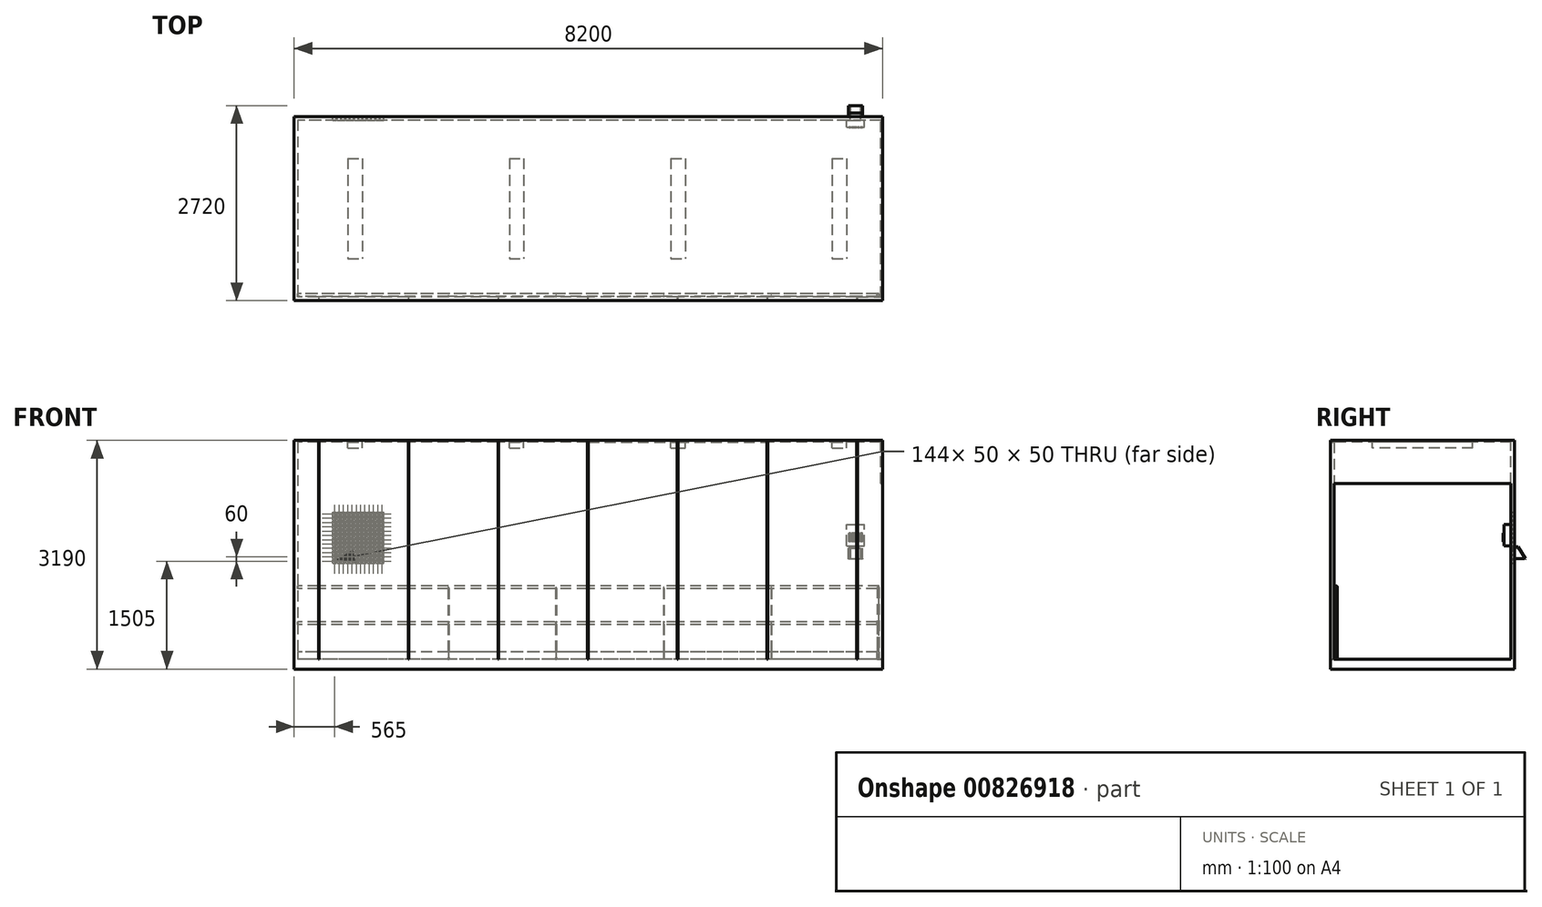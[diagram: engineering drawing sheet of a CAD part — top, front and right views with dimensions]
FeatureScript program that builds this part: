
annotation { "Feature Type Name" : "Feature", "Feature Type Description" : "" }
export const myFeature = defineFeature(function(context is Context, id is Id, definition is map)
    precondition{}
    {
        {
            var Q0;
            Q0=qCreatedBy(makeId("Top.planeOp"),FACE);
            var sketch = newSketch(context, id + "F0", { "sketchPlane" : qUnion([Q0])});
            skLineSegment(sketch, "E0.bottom", {"start": v(4100, -1285) * mm, "end": v(-4100, -1285) * mm});
            skLineSegment(sketch, "E0.top", {"start": v(4100, 1285) * mm, "end": v(-4100, 1285) * mm});
            skLineSegment(sketch, "E0.left", {"start": v(4100, -1285) * mm, "end": v(4100, 1285) * mm});
            skLineSegment(sketch, "E0.right", {"start": v(-4100, -1285) * mm, "end": v(-4100, 1285) * mm});
            skPoint(sketch, "E0.middle", {"position": v(0, 0) * mm});
            skSolve(sketch);
        }
        {
            var Q0;
            Q0=makeQuery(id+"F0.imprint","IMPRINT",FACE,{"disambiguationData":[TD([[makeQuery(id+"F0.imprint","IMPRINT",EDGE,{"derivedFrom":sQuery(id+"F0.wireOp",EDGE,"E0.bottom")}),-1.0]])]});
            extrude(context, id + "F1", {"entities" : qUnion([Q0]), "depth" : 25 * mm, "offsetDistance" : 25 * mm});
        }
        {
            var Q0;
            Q0=makeQuery(id+"F1.opExtrude","CAP_FACE",FACE,{"disambiguationData":[OSD([sQuery(id+"F0.wireOp",EDGE,"E0.bottom"),sQuery(id+"F0.wireOp",EDGE,"E0.top"),sQuery(id+"F0.wireOp",EDGE,"E0.left"),sQuery(id+"F0.wireOp",EDGE,"E0.right")])],"isStart":false});
            var sketch = newSketch(context, id + "F2", { "sketchPlane" : qUnion([Q0])});
            skLineSegment(sketch, "E1.bottom", {"start": v(4100, 1285) * mm, "end": v(-4100, 1285) * mm});
            skLineSegment(sketch, "E1.top", {"start": v(4100, 1235) * mm, "end": v(-4050, 1235) * mm});
            skLineSegment(sketch, "E1.left", {"start": v(4100, 1285) * mm, "end": v(4100, 1235) * mm});
            skLineSegment(sketch, "E1.right", {"start": v(-4100, 1285) * mm, "end": v(-4100, 1235) * mm});
            skLineSegment(sketch, "E2.bottom", {"start": v(-4100, 1285) * mm, "end": v(-4050, 1285) * mm});
            skLineSegment(sketch, "E2.top", {"start": v(-4100, -1285) * mm, "end": v(-4050, -1285) * mm});
            skLineSegment(sketch, "E2.left", {"start": v(-4100, 1285) * mm, "end": v(-4100, -1285) * mm});
            skLineSegment(sketch, "E2.right", {"start": v(-4050, 1235) * mm, "end": v(-4050, -1235) * mm});
            skLineSegment(sketch, "E3.bottom", {"start": v(-4100, -1285) * mm, "end": v(4100, -1285) * mm});
            skLineSegment(sketch, "E3.top", {"start": v(-4050, -1235) * mm, "end": v(4100, -1235) * mm});
            skLineSegment(sketch, "E3.left", {"start": v(-4100, -1285) * mm, "end": v(-4100, -1235) * mm});
            skLineSegment(sketch, "E3.right", {"start": v(4100, -1285) * mm, "end": v(4100, -1235) * mm});
            skLineSegment(sketch, "E4", {"start": v(-2510, -1235) * mm, "end": v(-2510, -1285) * mm});
            skLineSegment(sketch, "E5", {"start": v(-2510, -1285) * mm, "end": v(-2500, -1285) * mm});
            skLineSegment(sketch, "E6", {"start": v(-2500, -1285) * mm, "end": v(-2500, -1235) * mm});
            skLineSegment(sketch, "E7", {"start": v(-2500, -1235) * mm, "end": v(-2510, -1235) * mm});
            skLineSegment(sketch, "E8.1.0.0", {"start": v(-1260, -1235) * mm, "end": v(-1260, -1285) * mm});
            skLineSegment(sketch, "E8.1.0.1", {"start": v(-1250, -1285) * mm, "end": v(-1250, -1235) * mm});
            skLineSegment(sketch, "E8.1.0.2", {"start": v(-1250, -1235) * mm, "end": v(-1260, -1235) * mm});
            skLineSegment(sketch, "E8.1.0.3", {"start": v(-1260, -1285) * mm, "end": v(-1250, -1285) * mm});
            skLineSegment(sketch, "E8.2.0.0", {"start": v(-10, -1235) * mm, "end": v(-10, -1285) * mm});
            skLineSegment(sketch, "E8.2.0.1", {"start": v(0, -1285) * mm, "end": v(0, -1235) * mm});
            skLineSegment(sketch, "E8.2.0.2", {"start": v(0, -1235) * mm, "end": v(-10, -1235) * mm});
            skLineSegment(sketch, "E8.2.0.3", {"start": v(-10, -1285) * mm, "end": v(0, -1285) * mm});
            skLineSegment(sketch, "E8.3.0.0", {"start": v(1240, -1235) * mm, "end": v(1240, -1285) * mm});
            skLineSegment(sketch, "E8.3.0.1", {"start": v(1250, -1285) * mm, "end": v(1250, -1235) * mm});
            skLineSegment(sketch, "E8.3.0.2", {"start": v(1250, -1235) * mm, "end": v(1240, -1235) * mm});
            skLineSegment(sketch, "E8.3.0.3", {"start": v(1240, -1285) * mm, "end": v(1250, -1285) * mm});
            skLineSegment(sketch, "E8.4.0.0", {"start": v(2490, -1235) * mm, "end": v(2490, -1285) * mm});
            skLineSegment(sketch, "E8.4.0.1", {"start": v(2500, -1285) * mm, "end": v(2500, -1235) * mm});
            skLineSegment(sketch, "E8.4.0.2", {"start": v(2500, -1235) * mm, "end": v(2490, -1235) * mm});
            skLineSegment(sketch, "E8.4.0.3", {"start": v(2490, -1285) * mm, "end": v(2500, -1285) * mm});
            skLineSegment(sketch, "E8.direction1", {"start": v(-2510, -1285) * mm, "end": v(-1260, -1285) * mm, "construction": true});
            skLineSegment(sketch, "E9", {"start": v(-3750, -1285) * mm, "end": v(-3750, -1235) * mm});
            skLineSegment(sketch, "E10", {"start": v(-3750, -1235) * mm, "end": v(-4050, -1235) * mm});
            skLineSegment(sketch, "E11.0.5.0", {"start": v(3740, -1235) * mm, "end": v(3740, -1285) * mm});
            skLineSegment(sketch, "E11.3.5.0", {"start": v(3750, -1285) * mm, "end": v(3750, -1235) * mm});
            skLineSegment(sketch, "E11.6.5.0", {"start": v(3750, -1235) * mm, "end": v(3740, -1235) * mm});
            skLineSegment(sketch, "E11.9.5.0", {"start": v(3740, -1285) * mm, "end": v(3750, -1285) * mm});
            skLineSegment(sketch, "E12", {"start": v(-3760, -1235) * mm, "end": v(-3760, -1285) * mm});
            skSolve(sketch);
        }
        {
            var Q0;
            Q0=makeQuery(id+"F2.imprint","IMPRINT",FACE,{"disambiguationData":[TD([[makeQuery(id+"F2.imprint","IMPRINT",EDGE,{"derivedFrom":sQuery(id+"F2.wireOp",EDGE,"E1.bottom")}),1.0]])]});
            var Q1;
            {var subQ0=sQuery(id+"F2.wireOp",EDGE,"E4");Q1=makeQuery(id+"F2.imprint","IMPRINT",FACE,{"disambiguationData":[TD([[makeQuery(id+"F2.imprint","IMPRINT",EDGE,{"derivedFrom":subQ0}),-1.0]])]});}
            var Q2;
            {var subQ0=sQuery(id+"F2.wireOp",EDGE,"E6");Q2=makeQuery(id+"F2.imprint","IMPRINT",FACE,{"disambiguationData":[TD([[makeQuery(id+"F2.imprint","IMPRINT",EDGE,{"derivedFrom":subQ0}),-1.0]])]});}
            var Q3;
            {var subQ0=sQuery(id+"F2.wireOp",EDGE,"E8.1.0.1");Q3=makeQuery(id+"F2.imprint","IMPRINT",FACE,{"disambiguationData":[TD([[makeQuery(id+"F2.imprint","IMPRINT",EDGE,{"derivedFrom":subQ0}),-1.0]])]});}
            var Q4;
            {var subQ0=sQuery(id+"F2.wireOp",EDGE,"E8.2.0.1");Q4=makeQuery(id+"F2.imprint","IMPRINT",FACE,{"disambiguationData":[TD([[makeQuery(id+"F2.imprint","IMPRINT",EDGE,{"derivedFrom":subQ0}),-1.0]])]});}
            var Q5;
            {var subQ0=sQuery(id+"F2.wireOp",EDGE,"E8.3.0.1");Q5=makeQuery(id+"F2.imprint","IMPRINT",FACE,{"disambiguationData":[TD([[makeQuery(id+"F2.imprint","IMPRINT",EDGE,{"derivedFrom":subQ0}),-1.0]])]});}
            var Q6;
            {var subQ0=sQuery(id+"F2.wireOp",EDGE,"E3.right");Q6=makeQuery(id+"F2.imprint","IMPRINT",FACE,{"disambiguationData":[TD([[makeQuery(id+"F2.imprint","IMPRINT",EDGE,{"derivedFrom":subQ0}),1.0]])]});}
            var Q7;
            {var subQ0=sQuery(id+"F2.wireOp",EDGE,"E8.4.0.1");Q7=makeQuery(id+"F2.imprint","IMPRINT",FACE,{"disambiguationData":[TD([[makeQuery(id+"F2.imprint","IMPRINT",EDGE,{"derivedFrom":subQ0}),-1.0]])]});}
            extrude(context, id + "F3", {"entities" : qUnion([Q0, Q1, Q2, Q3, Q4, Q5, Q6, Q7]), "depth" : 3050 * mm, "offsetDistance" : 25 * mm});
        }
        {
            var Q0;
            Q0=makeQuery(id+"F3.opExtrude","CAP_FACE",FACE,{"disambiguationData":[OSD([sQuery(id+"F2.wireOp",EDGE,"E1.bottom"),sQuery(id+"F2.wireOp",EDGE,"E1.top"),sQuery(id+"F2.wireOp",EDGE,"E1.left"),sQuery(id+"F2.wireOp",EDGE,"E2.bottom"),sQuery(id+"F2.wireOp",EDGE,"E2.left"),sQuery(id+"F2.wireOp",EDGE,"E2.right"),sQuery(id+"F2.wireOp",EDGE,"E3.bottom"),sQuery(id+"F2.wireOp",EDGE,"E3.top"),sQuery(id+"F2.wireOp",EDGE,"E3.left"),sQuery(id+"F2.wireOp",EDGE,"E3.right")])],"isStart":false});
            var sketch = newSketch(context, id + "F4", { "sketchPlane" : qUnion([Q0])});
            skLineSegment(sketch, "E13.bottom", {"start": v(-4100, 1285) * mm, "end": v(4100, 1285) * mm});
            skLineSegment(sketch, "E13.top", {"start": v(-4100, -1285) * mm, "end": v(4100, -1285) * mm});
            skLineSegment(sketch, "E13.left", {"start": v(-4100, 1285) * mm, "end": v(-4100, -1285) * mm});
            skLineSegment(sketch, "E13.right", {"start": v(4100, 1285) * mm, "end": v(4100, -1285) * mm});
            skSolve(sketch);
        }
        {
            var Q0;
            Q0 = qSketchRegion(id + "F4", true);
            extrude(context, id + "F5", {"entities" : qUnion([Q0]), "operationType" : NewBodyOperationType.ADD, "oppositeDirection" : true, "depth" : 25 * mm, "offsetDistance" : 25 * mm});
        }
        {
            var Q0;
            Q0=makeQuery(id+"F5.boolean.opBoolean","MERGE",FACE,{"derivedFrom":[makeQuery(id+"F3.opExtrude","SWEPT_FACE",FACE,{"disambiguationData":[OSD([sQuery(id+"F2.wireOp",EDGE,"E1.left")])]}),makeQuery(id+"F3.opExtrude","SWEPT_FACE",FACE,{"disambiguationData":[OSD([sQuery(id+"F2.wireOp",EDGE,"E3.right")])]}),makeQuery(id+"F5.opExtrude","SWEPT_FACE",FACE,{"disambiguationData":[OSD([sQuery(id+"F4.wireOp",EDGE,"E13.right")])]})]});
            var sketch = newSketch(context, id + "F6", { "sketchPlane" : qUnion([Q0])});
            skLineSegment(sketch, "E14.bottom", {"start": v(-1285, 3075) * mm, "end": v(1285, 3075) * mm});
            skLineSegment(sketch, "E14.top", {"start": v(-1285, 2475) * mm, "end": v(1285, 2475) * mm});
            skLineSegment(sketch, "E14.left", {"start": v(-1285, 3075) * mm, "end": v(-1285, 2475) * mm});
            skLineSegment(sketch, "E14.right", {"start": v(1285, 3075) * mm, "end": v(1285, 2475) * mm});
            skSolve(sketch);
        }
        {
            var Q0;
            Q0 = qSketchRegion(id + "F6", true);
            extrude(context, id + "F7", {"entities" : qUnion([Q0]), "operationType" : NewBodyOperationType.ADD, "oppositeDirection" : true, "depth" : 25 * mm, "offsetDistance" : 25 * mm});
        }
        {
            var Q0;
            Q0=makeQuery(id+"F3.opExtrude","SWEPT_FACE",FACE,{"disambiguationData":[OSD([sQuery(id+"F2.wireOp",EDGE,"E2.right")])]});
            var sketch = newSketch(context, id + "F8", { "sketchPlane" : qUnion([Q0])});
            skLineSegment(sketch, "E15.bottom", {"start": v(-1235, 125) * mm, "end": v(-1225, 125) * mm});
            skLineSegment(sketch, "E15.top", {"start": v(-1235, 25) * mm, "end": v(-1225, 25) * mm});
            skLineSegment(sketch, "E15.left", {"start": v(-1235, 125) * mm, "end": v(-1235, 25) * mm});
            skLineSegment(sketch, "E15.right", {"start": v(-1225, 125) * mm, "end": v(-1225, 25) * mm});
            skCircle(sketch, "E16", {"center": v(-1205, 525) * mm, "radius": 20 * mm});
            skCircle(sketch, "E17", {"center": v(-1205, 1025) * mm, "radius": 20 * mm});
            skSolve(sketch);
        }
        {
            var Q0;
            Q0=makeQuery(id+"F8.imprint","IMPRINT",FACE,{"disambiguationData":[TD([[makeQuery(id+"F8.imprint","IMPRINT",EDGE,{"derivedFrom":sQuery(id+"F8.wireOp",EDGE,"E15.bottom")}),-1.0]])]});
            var Q1;
            Q1=makeQuery(id+"F8.imprint","IMPRINT",FACE,{"disambiguationData":[TD([[makeQuery(id+"F8.imprint","IMPRINT",EDGE,{"derivedFrom":sQuery(id+"F8.wireOp",EDGE,"E16")}),1.0]])]});
            var Q2;
            Q2=makeQuery(id+"F8.imprint","IMPRINT",FACE,{"disambiguationData":[TD([[makeQuery(id+"F8.imprint","IMPRINT",EDGE,{"derivedFrom":sQuery(id+"F8.wireOp",EDGE,"E17")}),1.0]])]});
            extrude(context, id + "F9", {"entities" : qUnion([Q0, Q1, Q2]), "operationType" : NewBodyOperationType.ADD, "depth" : 8100 * mm, "offsetDistance" : 25 * mm});
        }
        {
            var Q0;
            Q0=makeQuery(id+"F3.opExtrude","SWEPT_FACE",FACE,{"disambiguationData":[OSD([sQuery(id+"F2.wireOp",EDGE,"E1.top")])]});
            var sketch = newSketch(context, id + "F10", { "sketchPlane" : qUnion([Q0])});
            skLineSegment(sketch, "E18.bottom", {"start": v(4100, 25) * mm, "end": v(4090, 25) * mm});
            skLineSegment(sketch, "E18.top", {"start": v(4100, 125) * mm, "end": v(4090, 125) * mm});
            skLineSegment(sketch, "E18.left", {"start": v(4100, 25) * mm, "end": v(4100, 125) * mm});
            skLineSegment(sketch, "E18.right", {"start": v(4090, 25) * mm, "end": v(4090, 125) * mm});
            skSolve(sketch);
        }
        {
            var Q0;
            Q0=makeQuery(id+"F9.opExtrude","CAP_FACE",FACE,{"disambiguationData":[OSD([sQuery(id+"F8.wireOp",EDGE,"E17")])],"isStart":false});
            var sketch = newSketch(context, id + "F11", { "sketchPlane" : qUnion([Q0])});
            skLineSegment(sketch, "E19.bottom", {"start": v(-1225, 1024.55) * mm, "end": v(-1185, 1024.55) * mm});
            skLineSegment(sketch, "E19.top", {"start": v(-1225, 24.55) * mm, "end": v(-1185, 24.55) * mm});
            skLineSegment(sketch, "E19.left", {"start": v(-1225, 1024.55) * mm, "end": v(-1225, 24.55) * mm});
            skLineSegment(sketch, "E19.right", {"start": v(-1185, 1024.55) * mm, "end": v(-1185, 24.55) * mm});
            skSolve(sketch);
        }
        {
            var Q0;
            Q0 = qSketchRegion(id + "F11", true);
            extrude(context, id + "F12", {"entities" : qUnion([Q0]), "operationType" : NewBodyOperationType.ADD, "oppositeDirection" : true, "depth" : 25 * mm, "offsetDistance" : 25 * mm});
        }
        {
            var Q0;
            Q0=makeQuery(id+"F3.opExtrude","SWEPT_FACE",FACE,{"disambiguationData":[OSD([sQuery(id+"F2.wireOp",EDGE,"E1.bottom"),sQuery(id+"F2.wireOp",EDGE,"E2.bottom")])]});
            var sketch = newSketch(context, id + "F13", { "sketchPlane" : qUnion([Q0])});
            skLineSegment(sketch, "E20.bottom", {"start": v(-3650, 1425) * mm, "end": v(-3800, 1425) * mm});
            skLineSegment(sketch, "E20.top", {"start": v(-3650, 1575) * mm, "end": v(-3800, 1575) * mm});
            skLineSegment(sketch, "E20.left", {"start": v(-3650, 1425) * mm, "end": v(-3650, 1575) * mm});
            skLineSegment(sketch, "E20.right", {"start": v(-3800, 1425) * mm, "end": v(-3800, 1575) * mm});
            skPoint(sketch, "E20.middle", {"position": v(-3725, 1500) * mm});
            skSolve(sketch);
        }
        {
            var Q0;
            Q0=makeQuery(id+"F13.imprint","IMPRINT",FACE,{"disambiguationData":[TD([[makeQuery(id+"F13.imprint","IMPRINT",EDGE,{"derivedFrom":sQuery(id+"F13.wireOp",EDGE,"E20.bottom")}),-1.0]])]});
            extrude(context, id + "F14", {"entities" : qUnion([Q0]), "operationType" : NewBodyOperationType.REMOVE, "oppositeDirection" : true, "depth" : 50 * mm, "offsetDistance" : 25 * mm});
        }
        {
            var Q0;
            Q0=makeQuery(id+"F3.opExtrude","SWEPT_FACE",FACE,{"disambiguationData":[OSD([sQuery(id+"F2.wireOp",EDGE,"E1.bottom"),sQuery(id+"F2.wireOp",EDGE,"E2.bottom")])]});
            var sketch = newSketch(context, id + "F15", { "sketchPlane" : qUnion([Q0])});
            skLineSegment(sketch, "E21.top", {"start": v(-3625, 1595) * mm, "end": v(-3825, 1595) * mm});
            skLineSegment(sketch, "E21.left", {"start": v(-3625, 1425) * mm, "end": v(-3625, 1595) * mm});
            skLineSegment(sketch, "E21.right", {"start": v(-3825, 1425) * mm, "end": v(-3825, 1595) * mm});
            skPoint(sketch, "E21.middle", {"position": v(-3725, 1510) * mm});
            skLineSegment(sketch, "E22.0", {"start": v(-3650, 1575) * mm, "end": v(-3800, 1575) * mm});
            skLineSegment(sketch, "E23.0.0", {"start": v(-4100, 3075) * mm, "end": v(-4100, 25) * mm});
            skLineSegment(sketch, "E23.0.1", {"start": v(-4100, 25) * mm, "end": v(4100, 25) * mm});
            skLineSegment(sketch, "E23.0.2", {"start": v(4100, 25) * mm, "end": v(4100, 3075) * mm});
            skLineSegment(sketch, "E23.0.3", {"start": v(4100, 3075) * mm, "end": v(-4100, 3075) * mm});
            skLineSegment(sketch, "E24.0", {"start": v(-3800, 1425) * mm, "end": v(-3800, 1575) * mm});
            skLineSegment(sketch, "E25.0", {"start": v(-3650, 1425) * mm, "end": v(-3650, 1575) * mm});
            skLineSegment(sketch, "E26", {"start": v(-3825, 1425) * mm, "end": v(-3800, 1425) * mm});
            skLineSegment(sketch, "E27", {"start": v(-3650, 1425) * mm, "end": v(-3625, 1425) * mm});
            skSolve(sketch);
        }
        {
            var Q0;
            Q0=makeQuery(id+"F15.imprint","IMPRINT",FACE,{"disambiguationData":[TD([[makeQuery(id+"F15.imprint","IMPRINT",EDGE,{"derivedFrom":sQuery(id+"F15.wireOp",EDGE,"E21.top")}),1.0]])]});
            extrude(context, id + "F16", {"entities" : qUnion([Q0]), "operationType" : NewBodyOperationType.ADD, "depth" : 50 * mm, "offsetDistance" : 25 * mm});
        }
        {
            var Q0;
            Q0=makeQuery(id+"F16.opExtrude","SWEPT_FACE",FACE,{"disambiguationData":[OSD([sQuery(id+"F15.wireOp",EDGE,"E21.right")])]});
            var sketch = newSketch(context, id + "F17", { "sketchPlane" : qUnion([Q0])});
            skLineSegment(sketch, "E28", {"start": v(1335, 1595) * mm, "end": v(1435, 1425) * mm});
            skLineSegment(sketch, "E29", {"start": v(1435, 1425) * mm, "end": v(1335, 1425) * mm});
            skSolve(sketch);
        }
        {
            var Q0;
            Q0=makeQuery(id+"F17.imprint","IMPRINT",FACE,{"disambiguationData":[TD([[makeQuery(id+"F17.imprint","IMPRINT",EDGE,{"derivedFrom":sQuery(id+"F17.wireOp",EDGE,"E28")}),-1.0]])]});
            extrude(context, id + "F18", {"entities" : qUnion([Q0]), "operationType" : NewBodyOperationType.ADD, "oppositeDirection" : true, "depth" : 25 * mm, "offsetDistance" : 25 * mm});
        }
        {
            var Q0;
            Q0=makeQuery(id+"F16.opExtrude","SWEPT_FACE",FACE,{"disambiguationData":[OSD([sQuery(id+"F15.wireOp",EDGE,"E21.left")])]});
            var sketch = newSketch(context, id + "F19", { "sketchPlane" : qUnion([Q0])});
            skLineSegment(sketch, "E30.0", {"start": v(-1335, 1595) * mm, "end": v(-1435, 1425) * mm});
            skLineSegment(sketch, "E31.0", {"start": v(-1435, 1425) * mm, "end": v(-1285, 1425) * mm});
            skLineSegment(sketch, "E32.0", {"start": v(-1335, 1425) * mm, "end": v(-1335, 1595) * mm});
            skSolve(sketch);
        }
        {
            var Q0;
            {var subQ0=sQuery(id+"F19.wireOp",EDGE,"E30.0");Q0=makeQuery(id+"F19.imprint","IMPRINT",FACE,{"disambiguationData":[TD([[makeQuery(id+"F19.imprint","IMPRINT",EDGE,{"derivedFrom":subQ0}),1.0]])]});}
            extrude(context, id + "F20", {"entities" : qUnion([Q0]), "operationType" : NewBodyOperationType.ADD, "oppositeDirection" : true, "depth" : 25 * mm, "offsetDistance" : 25 * mm});
        }
        {
            var Q0;
            Q0=makeQuery(id+"F18.opExtrude","SWEPT_FACE",FACE,{"disambiguationData":[OSD([sQuery(id+"F17.wireOp",EDGE,"E28")])]});
            var sketch = newSketch(context, id + "F21", { "sketchPlane" : qUnion([Q0])});
            skLineSegment(sketch, "E33", {"start": v(-3825, 500.68) * mm, "end": v(-3625, 500.68) * mm});
            skLineSegment(sketch, "E34", {"start": v(-3625, 500.68) * mm, "end": v(-3625, 697.91) * mm});
            skLineSegment(sketch, "E35", {"start": v(-3625, 697.91) * mm, "end": v(-3825, 697.91) * mm});
            skLineSegment(sketch, "E36", {"start": v(-3825, 697.91) * mm, "end": v(-3825, 500.68) * mm});
            skSolve(sketch);
        }
        {
            var Q0;
            Q0 = qSketchRegion(id + "F21", true);
            extrude(context, id + "F22", {"entities" : qUnion([Q0]), "operationType" : NewBodyOperationType.ADD, "oppositeDirection" : true, "depth" : 10 * mm, "offsetDistance" : 25 * mm});
        }
        {
            var Q0;
            Q0=makeQuery(id+"F3.opExtrude","SWEPT_FACE",FACE,{"disambiguationData":[OSD([sQuery(id+"F2.wireOp",EDGE,"E1.bottom"),sQuery(id+"F2.wireOp",EDGE,"E2.bottom")])]});
            var sketch = newSketch(context, id + "F23", { "sketchPlane" : qUnion([Q0])});
            skPoint(sketch, "E37.middle", {"position": v(3200, 1725) * mm});
            skLineSegment(sketch, "E38.bottom", {"start": v(2900, 2025) * mm, "end": v(2850, 2025) * mm});
            skLineSegment(sketch, "E38.top", {"start": v(2900, 2075) * mm, "end": v(2850, 2075) * mm});
            skLineSegment(sketch, "E38.left", {"start": v(2900, 2025) * mm, "end": v(2900, 2075) * mm});
            skLineSegment(sketch, "E38.right", {"start": v(2850, 2025) * mm, "end": v(2850, 2075) * mm});
            skPoint(sketch, "E38.middle", {"position": v(2875, 2050) * mm});
            skLineSegment(sketch, "E39.0.1.0", {"start": v(2850, 1965) * mm, "end": v(2850, 2015) * mm});
            skLineSegment(sketch, "E39.0.1.1", {"start": v(2900, 2015) * mm, "end": v(2850, 2015) * mm});
            skPoint(sketch, "E39.0.1.2", {"position": v(2875, 1990) * mm});
            skLineSegment(sketch, "E39.0.1.3", {"start": v(2900, 1965) * mm, "end": v(2850, 1965) * mm});
            skLineSegment(sketch, "E39.0.1.4", {"start": v(2900, 1965) * mm, "end": v(2900, 2015) * mm});
            skLineSegment(sketch, "E39.0.2.0", {"start": v(2850, 1905) * mm, "end": v(2850, 1955) * mm});
            skLineSegment(sketch, "E39.0.2.1", {"start": v(2900, 1955) * mm, "end": v(2850, 1955) * mm});
            skPoint(sketch, "E39.0.2.2", {"position": v(2875, 1930) * mm});
            skLineSegment(sketch, "E39.0.2.3", {"start": v(2900, 1905) * mm, "end": v(2850, 1905) * mm});
            skLineSegment(sketch, "E39.0.2.4", {"start": v(2900, 1905) * mm, "end": v(2900, 1955) * mm});
            skLineSegment(sketch, "E39.0.3.0", {"start": v(2850, 1845) * mm, "end": v(2850, 1895) * mm});
            skLineSegment(sketch, "E39.0.3.1", {"start": v(2900, 1895) * mm, "end": v(2850, 1895) * mm});
            skPoint(sketch, "E39.0.3.2", {"position": v(2875, 1870) * mm});
            skLineSegment(sketch, "E39.0.3.3", {"start": v(2900, 1845) * mm, "end": v(2850, 1845) * mm});
            skLineSegment(sketch, "E39.0.3.4", {"start": v(2900, 1845) * mm, "end": v(2900, 1895) * mm});
            skLineSegment(sketch, "E39.0.4.0", {"start": v(2850, 1785) * mm, "end": v(2850, 1835) * mm});
            skLineSegment(sketch, "E39.0.4.1", {"start": v(2900, 1835) * mm, "end": v(2850, 1835) * mm});
            skPoint(sketch, "E39.0.4.2", {"position": v(2875, 1810) * mm});
            skLineSegment(sketch, "E39.0.4.3", {"start": v(2900, 1785) * mm, "end": v(2850, 1785) * mm});
            skLineSegment(sketch, "E39.0.4.4", {"start": v(2900, 1785) * mm, "end": v(2900, 1835) * mm});
            skLineSegment(sketch, "E39.0.5.0", {"start": v(2850, 1725) * mm, "end": v(2850, 1775) * mm});
            skLineSegment(sketch, "E39.0.5.1", {"start": v(2900, 1775) * mm, "end": v(2850, 1775) * mm});
            skPoint(sketch, "E39.0.5.2", {"position": v(2875, 1750) * mm});
            skLineSegment(sketch, "E39.0.5.3", {"start": v(2900, 1725) * mm, "end": v(2850, 1725) * mm});
            skLineSegment(sketch, "E39.0.5.4", {"start": v(2900, 1725) * mm, "end": v(2900, 1775) * mm});
            skLineSegment(sketch, "E39.0.6.0", {"start": v(2850, 1665) * mm, "end": v(2850, 1715) * mm});
            skLineSegment(sketch, "E39.0.6.1", {"start": v(2900, 1715) * mm, "end": v(2850, 1715) * mm});
            skPoint(sketch, "E39.0.6.2", {"position": v(2875, 1690) * mm});
            skLineSegment(sketch, "E39.0.6.3", {"start": v(2900, 1665) * mm, "end": v(2850, 1665) * mm});
            skLineSegment(sketch, "E39.0.6.4", {"start": v(2900, 1665) * mm, "end": v(2900, 1715) * mm});
            skLineSegment(sketch, "E39.0.7.0", {"start": v(2850, 1605) * mm, "end": v(2850, 1655) * mm});
            skLineSegment(sketch, "E39.0.7.1", {"start": v(2900, 1655) * mm, "end": v(2850, 1655) * mm});
            skPoint(sketch, "E39.0.7.2", {"position": v(2875, 1630) * mm});
            skLineSegment(sketch, "E39.0.7.3", {"start": v(2900, 1605) * mm, "end": v(2850, 1605) * mm});
            skLineSegment(sketch, "E39.0.7.4", {"start": v(2900, 1605) * mm, "end": v(2900, 1655) * mm});
            skLineSegment(sketch, "E39.0.8.0", {"start": v(2850, 1545) * mm, "end": v(2850, 1595) * mm});
            skLineSegment(sketch, "E39.0.8.1", {"start": v(2900, 1595) * mm, "end": v(2850, 1595) * mm});
            skPoint(sketch, "E39.0.8.2", {"position": v(2875, 1570) * mm});
            skLineSegment(sketch, "E39.0.8.3", {"start": v(2900, 1545) * mm, "end": v(2850, 1545) * mm});
            skLineSegment(sketch, "E39.0.8.4", {"start": v(2900, 1545) * mm, "end": v(2900, 1595) * mm});
            skLineSegment(sketch, "E39.0.9.0", {"start": v(2850, 1485) * mm, "end": v(2850, 1535) * mm});
            skLineSegment(sketch, "E39.0.9.1", {"start": v(2900, 1535) * mm, "end": v(2850, 1535) * mm});
            skPoint(sketch, "E39.0.9.2", {"position": v(2875, 1510) * mm});
            skLineSegment(sketch, "E39.0.9.3", {"start": v(2900, 1485) * mm, "end": v(2850, 1485) * mm});
            skLineSegment(sketch, "E39.0.9.4", {"start": v(2900, 1485) * mm, "end": v(2900, 1535) * mm});
            skLineSegment(sketch, "E39.0.10.0", {"start": v(2850, 1425) * mm, "end": v(2850, 1475) * mm});
            skLineSegment(sketch, "E39.0.10.1", {"start": v(2900, 1475) * mm, "end": v(2850, 1475) * mm});
            skPoint(sketch, "E39.0.10.2", {"position": v(2875, 1450) * mm});
            skLineSegment(sketch, "E39.0.10.3", {"start": v(2900, 1425) * mm, "end": v(2850, 1425) * mm});
            skLineSegment(sketch, "E39.0.10.4", {"start": v(2900, 1425) * mm, "end": v(2900, 1475) * mm});
            skLineSegment(sketch, "E39.0.11.0", {"start": v(2850, 1365) * mm, "end": v(2850, 1415) * mm});
            skLineSegment(sketch, "E39.0.11.1", {"start": v(2900, 1415) * mm, "end": v(2850, 1415) * mm});
            skPoint(sketch, "E39.0.11.2", {"position": v(2875, 1390) * mm});
            skLineSegment(sketch, "E39.0.11.3", {"start": v(2900, 1365) * mm, "end": v(2850, 1365) * mm});
            skLineSegment(sketch, "E39.0.11.4", {"start": v(2900, 1365) * mm, "end": v(2900, 1415) * mm});
            skLineSegment(sketch, "E39.1.0.0", {"start": v(2910, 2025) * mm, "end": v(2910, 2075) * mm});
            skLineSegment(sketch, "E39.1.0.1", {"start": v(2960, 2075) * mm, "end": v(2910, 2075) * mm});
            skPoint(sketch, "E39.1.0.2", {"position": v(2935, 2050) * mm});
            skLineSegment(sketch, "E39.1.0.3", {"start": v(2960, 2025) * mm, "end": v(2910, 2025) * mm});
            skLineSegment(sketch, "E39.1.0.4", {"start": v(2960, 2025) * mm, "end": v(2960, 2075) * mm});
            skLineSegment(sketch, "E39.1.1.0", {"start": v(2910, 1965) * mm, "end": v(2910, 2015) * mm});
            skLineSegment(sketch, "E39.1.1.1", {"start": v(2960, 2015) * mm, "end": v(2910, 2015) * mm});
            skPoint(sketch, "E39.1.1.2", {"position": v(2935, 1990) * mm});
            skLineSegment(sketch, "E39.1.1.3", {"start": v(2960, 1965) * mm, "end": v(2910, 1965) * mm});
            skLineSegment(sketch, "E39.1.1.4", {"start": v(2960, 1965) * mm, "end": v(2960, 2015) * mm});
            skLineSegment(sketch, "E39.1.2.0", {"start": v(2910, 1905) * mm, "end": v(2910, 1955) * mm});
            skLineSegment(sketch, "E39.1.2.1", {"start": v(2960, 1955) * mm, "end": v(2910, 1955) * mm});
            skPoint(sketch, "E39.1.2.2", {"position": v(2935, 1930) * mm});
            skLineSegment(sketch, "E39.1.2.3", {"start": v(2960, 1905) * mm, "end": v(2910, 1905) * mm});
            skLineSegment(sketch, "E39.1.2.4", {"start": v(2960, 1905) * mm, "end": v(2960, 1955) * mm});
            skLineSegment(sketch, "E39.1.3.0", {"start": v(2910, 1845) * mm, "end": v(2910, 1895) * mm});
            skLineSegment(sketch, "E39.1.3.1", {"start": v(2960, 1895) * mm, "end": v(2910, 1895) * mm});
            skPoint(sketch, "E39.1.3.2", {"position": v(2935, 1870) * mm});
            skLineSegment(sketch, "E39.1.3.3", {"start": v(2960, 1845) * mm, "end": v(2910, 1845) * mm});
            skLineSegment(sketch, "E39.1.3.4", {"start": v(2960, 1845) * mm, "end": v(2960, 1895) * mm});
            skLineSegment(sketch, "E39.1.4.0", {"start": v(2910, 1785) * mm, "end": v(2910, 1835) * mm});
            skLineSegment(sketch, "E39.1.4.1", {"start": v(2960, 1835) * mm, "end": v(2910, 1835) * mm});
            skPoint(sketch, "E39.1.4.2", {"position": v(2935, 1810) * mm});
            skLineSegment(sketch, "E39.1.4.3", {"start": v(2960, 1785) * mm, "end": v(2910, 1785) * mm});
            skLineSegment(sketch, "E39.1.4.4", {"start": v(2960, 1785) * mm, "end": v(2960, 1835) * mm});
            skLineSegment(sketch, "E39.1.5.0", {"start": v(2910, 1725) * mm, "end": v(2910, 1775) * mm});
            skLineSegment(sketch, "E39.1.5.1", {"start": v(2960, 1775) * mm, "end": v(2910, 1775) * mm});
            skPoint(sketch, "E39.1.5.2", {"position": v(2935, 1750) * mm});
            skLineSegment(sketch, "E39.1.5.3", {"start": v(2960, 1725) * mm, "end": v(2910, 1725) * mm});
            skLineSegment(sketch, "E39.1.5.4", {"start": v(2960, 1725) * mm, "end": v(2960, 1775) * mm});
            skLineSegment(sketch, "E39.1.6.0", {"start": v(2910, 1665) * mm, "end": v(2910, 1715) * mm});
            skLineSegment(sketch, "E39.1.6.1", {"start": v(2960, 1715) * mm, "end": v(2910, 1715) * mm});
            skPoint(sketch, "E39.1.6.2", {"position": v(2935, 1690) * mm});
            skLineSegment(sketch, "E39.1.6.3", {"start": v(2960, 1665) * mm, "end": v(2910, 1665) * mm});
            skLineSegment(sketch, "E39.1.6.4", {"start": v(2960, 1665) * mm, "end": v(2960, 1715) * mm});
            skLineSegment(sketch, "E39.1.7.0", {"start": v(2910, 1605) * mm, "end": v(2910, 1655) * mm});
            skLineSegment(sketch, "E39.1.7.1", {"start": v(2960, 1655) * mm, "end": v(2910, 1655) * mm});
            skPoint(sketch, "E39.1.7.2", {"position": v(2935, 1630) * mm});
            skLineSegment(sketch, "E39.1.7.3", {"start": v(2960, 1605) * mm, "end": v(2910, 1605) * mm});
            skLineSegment(sketch, "E39.1.7.4", {"start": v(2960, 1605) * mm, "end": v(2960, 1655) * mm});
            skLineSegment(sketch, "E39.1.8.0", {"start": v(2910, 1545) * mm, "end": v(2910, 1595) * mm});
            skLineSegment(sketch, "E39.1.8.1", {"start": v(2960, 1595) * mm, "end": v(2910, 1595) * mm});
            skPoint(sketch, "E39.1.8.2", {"position": v(2935, 1570) * mm});
            skLineSegment(sketch, "E39.1.8.3", {"start": v(2960, 1545) * mm, "end": v(2910, 1545) * mm});
            skLineSegment(sketch, "E39.1.8.4", {"start": v(2960, 1545) * mm, "end": v(2960, 1595) * mm});
            skLineSegment(sketch, "E39.1.9.0", {"start": v(2910, 1485) * mm, "end": v(2910, 1535) * mm});
            skLineSegment(sketch, "E39.1.9.1", {"start": v(2960, 1535) * mm, "end": v(2910, 1535) * mm});
            skPoint(sketch, "E39.1.9.2", {"position": v(2935, 1510) * mm});
            skLineSegment(sketch, "E39.1.9.3", {"start": v(2960, 1485) * mm, "end": v(2910, 1485) * mm});
            skLineSegment(sketch, "E39.1.9.4", {"start": v(2960, 1485) * mm, "end": v(2960, 1535) * mm});
            skLineSegment(sketch, "E39.1.10.0", {"start": v(2910, 1425) * mm, "end": v(2910, 1475) * mm});
            skLineSegment(sketch, "E39.1.10.1", {"start": v(2960, 1475) * mm, "end": v(2910, 1475) * mm});
            skPoint(sketch, "E39.1.10.2", {"position": v(2935, 1450) * mm});
            skLineSegment(sketch, "E39.1.10.3", {"start": v(2960, 1425) * mm, "end": v(2910, 1425) * mm});
            skLineSegment(sketch, "E39.1.10.4", {"start": v(2960, 1425) * mm, "end": v(2960, 1475) * mm});
            skLineSegment(sketch, "E39.1.11.0", {"start": v(2910, 1365) * mm, "end": v(2910, 1415) * mm});
            skLineSegment(sketch, "E39.1.11.1", {"start": v(2960, 1415) * mm, "end": v(2910, 1415) * mm});
            skPoint(sketch, "E39.1.11.2", {"position": v(2935, 1390) * mm});
            skLineSegment(sketch, "E39.1.11.3", {"start": v(2960, 1365) * mm, "end": v(2910, 1365) * mm});
            skLineSegment(sketch, "E39.1.11.4", {"start": v(2960, 1365) * mm, "end": v(2960, 1415) * mm});
            skLineSegment(sketch, "E39.2.0.0", {"start": v(2970, 2025) * mm, "end": v(2970, 2075) * mm});
            skLineSegment(sketch, "E39.2.0.1", {"start": v(3020, 2075) * mm, "end": v(2970, 2075) * mm});
            skPoint(sketch, "E39.2.0.2", {"position": v(2995, 2050) * mm});
            skLineSegment(sketch, "E39.2.0.3", {"start": v(3020, 2025) * mm, "end": v(2970, 2025) * mm});
            skLineSegment(sketch, "E39.2.0.4", {"start": v(3020, 2025) * mm, "end": v(3020, 2075) * mm});
            skLineSegment(sketch, "E39.2.1.0", {"start": v(2970, 1965) * mm, "end": v(2970, 2015) * mm});
            skLineSegment(sketch, "E39.2.1.1", {"start": v(3020, 2015) * mm, "end": v(2970, 2015) * mm});
            skPoint(sketch, "E39.2.1.2", {"position": v(2995, 1990) * mm});
            skLineSegment(sketch, "E39.2.1.3", {"start": v(3020, 1965) * mm, "end": v(2970, 1965) * mm});
            skLineSegment(sketch, "E39.2.1.4", {"start": v(3020, 1965) * mm, "end": v(3020, 2015) * mm});
            skLineSegment(sketch, "E39.2.2.0", {"start": v(2970, 1905) * mm, "end": v(2970, 1955) * mm});
            skLineSegment(sketch, "E39.2.2.1", {"start": v(3020, 1955) * mm, "end": v(2970, 1955) * mm});
            skPoint(sketch, "E39.2.2.2", {"position": v(2995, 1930) * mm});
            skLineSegment(sketch, "E39.2.2.3", {"start": v(3020, 1905) * mm, "end": v(2970, 1905) * mm});
            skLineSegment(sketch, "E39.2.2.4", {"start": v(3020, 1905) * mm, "end": v(3020, 1955) * mm});
            skLineSegment(sketch, "E39.2.3.0", {"start": v(2970, 1845) * mm, "end": v(2970, 1895) * mm});
            skLineSegment(sketch, "E39.2.3.1", {"start": v(3020, 1895) * mm, "end": v(2970, 1895) * mm});
            skPoint(sketch, "E39.2.3.2", {"position": v(2995, 1870) * mm});
            skLineSegment(sketch, "E39.2.3.3", {"start": v(3020, 1845) * mm, "end": v(2970, 1845) * mm});
            skLineSegment(sketch, "E39.2.3.4", {"start": v(3020, 1845) * mm, "end": v(3020, 1895) * mm});
            skLineSegment(sketch, "E39.2.4.0", {"start": v(2970, 1785) * mm, "end": v(2970, 1835) * mm});
            skLineSegment(sketch, "E39.2.4.1", {"start": v(3020, 1835) * mm, "end": v(2970, 1835) * mm});
            skPoint(sketch, "E39.2.4.2", {"position": v(2995, 1810) * mm});
            skLineSegment(sketch, "E39.2.4.3", {"start": v(3020, 1785) * mm, "end": v(2970, 1785) * mm});
            skLineSegment(sketch, "E39.2.4.4", {"start": v(3020, 1785) * mm, "end": v(3020, 1835) * mm});
            skLineSegment(sketch, "E39.2.5.0", {"start": v(2970, 1725) * mm, "end": v(2970, 1775) * mm});
            skLineSegment(sketch, "E39.2.5.1", {"start": v(3020, 1775) * mm, "end": v(2970, 1775) * mm});
            skPoint(sketch, "E39.2.5.2", {"position": v(2995, 1750) * mm});
            skLineSegment(sketch, "E39.2.5.3", {"start": v(3020, 1725) * mm, "end": v(2970, 1725) * mm});
            skLineSegment(sketch, "E39.2.5.4", {"start": v(3020, 1725) * mm, "end": v(3020, 1775) * mm});
            skLineSegment(sketch, "E39.2.6.0", {"start": v(2970, 1665) * mm, "end": v(2970, 1715) * mm});
            skLineSegment(sketch, "E39.2.6.1", {"start": v(3020, 1715) * mm, "end": v(2970, 1715) * mm});
            skPoint(sketch, "E39.2.6.2", {"position": v(2995, 1690) * mm});
            skLineSegment(sketch, "E39.2.6.3", {"start": v(3020, 1665) * mm, "end": v(2970, 1665) * mm});
            skLineSegment(sketch, "E39.2.6.4", {"start": v(3020, 1665) * mm, "end": v(3020, 1715) * mm});
            skLineSegment(sketch, "E39.2.7.0", {"start": v(2970, 1605) * mm, "end": v(2970, 1655) * mm});
            skLineSegment(sketch, "E39.2.7.1", {"start": v(3020, 1655) * mm, "end": v(2970, 1655) * mm});
            skPoint(sketch, "E39.2.7.2", {"position": v(2995, 1630) * mm});
            skLineSegment(sketch, "E39.2.7.3", {"start": v(3020, 1605) * mm, "end": v(2970, 1605) * mm});
            skLineSegment(sketch, "E39.2.7.4", {"start": v(3020, 1605) * mm, "end": v(3020, 1655) * mm});
            skLineSegment(sketch, "E39.2.8.0", {"start": v(2970, 1545) * mm, "end": v(2970, 1595) * mm});
            skLineSegment(sketch, "E39.2.8.1", {"start": v(3020, 1595) * mm, "end": v(2970, 1595) * mm});
            skPoint(sketch, "E39.2.8.2", {"position": v(2995, 1570) * mm});
            skLineSegment(sketch, "E39.2.8.3", {"start": v(3020, 1545) * mm, "end": v(2970, 1545) * mm});
            skLineSegment(sketch, "E39.2.8.4", {"start": v(3020, 1545) * mm, "end": v(3020, 1595) * mm});
            skLineSegment(sketch, "E39.2.9.0", {"start": v(2970, 1485) * mm, "end": v(2970, 1535) * mm});
            skLineSegment(sketch, "E39.2.9.1", {"start": v(3020, 1535) * mm, "end": v(2970, 1535) * mm});
            skPoint(sketch, "E39.2.9.2", {"position": v(2995, 1510) * mm});
            skLineSegment(sketch, "E39.2.9.3", {"start": v(3020, 1485) * mm, "end": v(2970, 1485) * mm});
            skLineSegment(sketch, "E39.2.9.4", {"start": v(3020, 1485) * mm, "end": v(3020, 1535) * mm});
            skLineSegment(sketch, "E39.2.10.0", {"start": v(2970, 1425) * mm, "end": v(2970, 1475) * mm});
            skLineSegment(sketch, "E39.2.10.1", {"start": v(3020, 1475) * mm, "end": v(2970, 1475) * mm});
            skPoint(sketch, "E39.2.10.2", {"position": v(2995, 1450) * mm});
            skLineSegment(sketch, "E39.2.10.3", {"start": v(3020, 1425) * mm, "end": v(2970, 1425) * mm});
            skLineSegment(sketch, "E39.2.10.4", {"start": v(3020, 1425) * mm, "end": v(3020, 1475) * mm});
            skLineSegment(sketch, "E39.2.11.0", {"start": v(2970, 1365) * mm, "end": v(2970, 1415) * mm});
            skLineSegment(sketch, "E39.2.11.1", {"start": v(3020, 1415) * mm, "end": v(2970, 1415) * mm});
            skPoint(sketch, "E39.2.11.2", {"position": v(2995, 1390) * mm});
            skLineSegment(sketch, "E39.2.11.3", {"start": v(3020, 1365) * mm, "end": v(2970, 1365) * mm});
            skLineSegment(sketch, "E39.2.11.4", {"start": v(3020, 1365) * mm, "end": v(3020, 1415) * mm});
            skLineSegment(sketch, "E39.3.0.0", {"start": v(3030, 2025) * mm, "end": v(3030, 2075) * mm});
            skLineSegment(sketch, "E39.3.0.1", {"start": v(3080, 2075) * mm, "end": v(3030, 2075) * mm});
            skPoint(sketch, "E39.3.0.2", {"position": v(3055, 2050) * mm});
            skLineSegment(sketch, "E39.3.0.3", {"start": v(3080, 2025) * mm, "end": v(3030, 2025) * mm});
            skLineSegment(sketch, "E39.3.0.4", {"start": v(3080, 2025) * mm, "end": v(3080, 2075) * mm});
            skLineSegment(sketch, "E39.3.1.0", {"start": v(3030, 1965) * mm, "end": v(3030, 2015) * mm});
            skLineSegment(sketch, "E39.3.1.1", {"start": v(3080, 2015) * mm, "end": v(3030, 2015) * mm});
            skPoint(sketch, "E39.3.1.2", {"position": v(3055, 1990) * mm});
            skLineSegment(sketch, "E39.3.1.3", {"start": v(3080, 1965) * mm, "end": v(3030, 1965) * mm});
            skLineSegment(sketch, "E39.3.1.4", {"start": v(3080, 1965) * mm, "end": v(3080, 2015) * mm});
            skLineSegment(sketch, "E39.3.2.0", {"start": v(3030, 1905) * mm, "end": v(3030, 1955) * mm});
            skLineSegment(sketch, "E39.3.2.1", {"start": v(3080, 1955) * mm, "end": v(3030, 1955) * mm});
            skPoint(sketch, "E39.3.2.2", {"position": v(3055, 1930) * mm});
            skLineSegment(sketch, "E39.3.2.3", {"start": v(3080, 1905) * mm, "end": v(3030, 1905) * mm});
            skLineSegment(sketch, "E39.3.2.4", {"start": v(3080, 1905) * mm, "end": v(3080, 1955) * mm});
            skLineSegment(sketch, "E39.3.3.0", {"start": v(3030, 1845) * mm, "end": v(3030, 1895) * mm});
            skLineSegment(sketch, "E39.3.3.1", {"start": v(3080, 1895) * mm, "end": v(3030, 1895) * mm});
            skPoint(sketch, "E39.3.3.2", {"position": v(3055, 1870) * mm});
            skLineSegment(sketch, "E39.3.3.3", {"start": v(3080, 1845) * mm, "end": v(3030, 1845) * mm});
            skLineSegment(sketch, "E39.3.3.4", {"start": v(3080, 1845) * mm, "end": v(3080, 1895) * mm});
            skLineSegment(sketch, "E39.3.4.0", {"start": v(3030, 1785) * mm, "end": v(3030, 1835) * mm});
            skLineSegment(sketch, "E39.3.4.1", {"start": v(3080, 1835) * mm, "end": v(3030, 1835) * mm});
            skPoint(sketch, "E39.3.4.2", {"position": v(3055, 1810) * mm});
            skLineSegment(sketch, "E39.3.4.3", {"start": v(3080, 1785) * mm, "end": v(3030, 1785) * mm});
            skLineSegment(sketch, "E39.3.4.4", {"start": v(3080, 1785) * mm, "end": v(3080, 1835) * mm});
            skLineSegment(sketch, "E39.3.5.0", {"start": v(3030, 1725) * mm, "end": v(3030, 1775) * mm});
            skLineSegment(sketch, "E39.3.5.1", {"start": v(3080, 1775) * mm, "end": v(3030, 1775) * mm});
            skPoint(sketch, "E39.3.5.2", {"position": v(3055, 1750) * mm});
            skLineSegment(sketch, "E39.3.5.3", {"start": v(3080, 1725) * mm, "end": v(3030, 1725) * mm});
            skLineSegment(sketch, "E39.3.5.4", {"start": v(3080, 1725) * mm, "end": v(3080, 1775) * mm});
            skLineSegment(sketch, "E39.3.6.0", {"start": v(3030, 1665) * mm, "end": v(3030, 1715) * mm});
            skLineSegment(sketch, "E39.3.6.1", {"start": v(3080, 1715) * mm, "end": v(3030, 1715) * mm});
            skPoint(sketch, "E39.3.6.2", {"position": v(3055, 1690) * mm});
            skLineSegment(sketch, "E39.3.6.3", {"start": v(3080, 1665) * mm, "end": v(3030, 1665) * mm});
            skLineSegment(sketch, "E39.3.6.4", {"start": v(3080, 1665) * mm, "end": v(3080, 1715) * mm});
            skLineSegment(sketch, "E39.3.7.0", {"start": v(3030, 1605) * mm, "end": v(3030, 1655) * mm});
            skLineSegment(sketch, "E39.3.7.1", {"start": v(3080, 1655) * mm, "end": v(3030, 1655) * mm});
            skPoint(sketch, "E39.3.7.2", {"position": v(3055, 1630) * mm});
            skLineSegment(sketch, "E39.3.7.3", {"start": v(3080, 1605) * mm, "end": v(3030, 1605) * mm});
            skLineSegment(sketch, "E39.3.7.4", {"start": v(3080, 1605) * mm, "end": v(3080, 1655) * mm});
            skLineSegment(sketch, "E39.3.8.0", {"start": v(3030, 1545) * mm, "end": v(3030, 1595) * mm});
            skLineSegment(sketch, "E39.3.8.1", {"start": v(3080, 1595) * mm, "end": v(3030, 1595) * mm});
            skPoint(sketch, "E39.3.8.2", {"position": v(3055, 1570) * mm});
            skLineSegment(sketch, "E39.3.8.3", {"start": v(3080, 1545) * mm, "end": v(3030, 1545) * mm});
            skLineSegment(sketch, "E39.3.8.4", {"start": v(3080, 1545) * mm, "end": v(3080, 1595) * mm});
            skLineSegment(sketch, "E39.3.9.0", {"start": v(3030, 1485) * mm, "end": v(3030, 1535) * mm});
            skLineSegment(sketch, "E39.3.9.1", {"start": v(3080, 1535) * mm, "end": v(3030, 1535) * mm});
            skPoint(sketch, "E39.3.9.2", {"position": v(3055, 1510) * mm});
            skLineSegment(sketch, "E39.3.9.3", {"start": v(3080, 1485) * mm, "end": v(3030, 1485) * mm});
            skLineSegment(sketch, "E39.3.9.4", {"start": v(3080, 1485) * mm, "end": v(3080, 1535) * mm});
            skLineSegment(sketch, "E39.3.10.0", {"start": v(3030, 1425) * mm, "end": v(3030, 1475) * mm});
            skLineSegment(sketch, "E39.3.10.1", {"start": v(3080, 1475) * mm, "end": v(3030, 1475) * mm});
            skPoint(sketch, "E39.3.10.2", {"position": v(3055, 1450) * mm});
            skLineSegment(sketch, "E39.3.10.3", {"start": v(3080, 1425) * mm, "end": v(3030, 1425) * mm});
            skLineSegment(sketch, "E39.3.10.4", {"start": v(3080, 1425) * mm, "end": v(3080, 1475) * mm});
            skLineSegment(sketch, "E39.3.11.0", {"start": v(3030, 1365) * mm, "end": v(3030, 1415) * mm});
            skLineSegment(sketch, "E39.3.11.1", {"start": v(3080, 1415) * mm, "end": v(3030, 1415) * mm});
            skPoint(sketch, "E39.3.11.2", {"position": v(3055, 1390) * mm});
            skLineSegment(sketch, "E39.3.11.3", {"start": v(3080, 1365) * mm, "end": v(3030, 1365) * mm});
            skLineSegment(sketch, "E39.3.11.4", {"start": v(3080, 1365) * mm, "end": v(3080, 1415) * mm});
            skLineSegment(sketch, "E39.4.0.0", {"start": v(3090, 2025) * mm, "end": v(3090, 2075) * mm});
            skLineSegment(sketch, "E39.4.0.1", {"start": v(3140, 2075) * mm, "end": v(3090, 2075) * mm});
            skPoint(sketch, "E39.4.0.2", {"position": v(3115, 2050) * mm});
            skLineSegment(sketch, "E39.4.0.3", {"start": v(3140, 2025) * mm, "end": v(3090, 2025) * mm});
            skLineSegment(sketch, "E39.4.0.4", {"start": v(3140, 2025) * mm, "end": v(3140, 2075) * mm});
            skLineSegment(sketch, "E39.4.1.0", {"start": v(3090, 1965) * mm, "end": v(3090, 2015) * mm});
            skLineSegment(sketch, "E39.4.1.1", {"start": v(3140, 2015) * mm, "end": v(3090, 2015) * mm});
            skPoint(sketch, "E39.4.1.2", {"position": v(3115, 1990) * mm});
            skLineSegment(sketch, "E39.4.1.3", {"start": v(3140, 1965) * mm, "end": v(3090, 1965) * mm});
            skLineSegment(sketch, "E39.4.1.4", {"start": v(3140, 1965) * mm, "end": v(3140, 2015) * mm});
            skLineSegment(sketch, "E39.4.2.0", {"start": v(3090, 1905) * mm, "end": v(3090, 1955) * mm});
            skLineSegment(sketch, "E39.4.2.1", {"start": v(3140, 1955) * mm, "end": v(3090, 1955) * mm});
            skPoint(sketch, "E39.4.2.2", {"position": v(3115, 1930) * mm});
            skLineSegment(sketch, "E39.4.2.3", {"start": v(3140, 1905) * mm, "end": v(3090, 1905) * mm});
            skLineSegment(sketch, "E39.4.2.4", {"start": v(3140, 1905) * mm, "end": v(3140, 1955) * mm});
            skLineSegment(sketch, "E39.4.3.0", {"start": v(3090, 1845) * mm, "end": v(3090, 1895) * mm});
            skLineSegment(sketch, "E39.4.3.1", {"start": v(3140, 1895) * mm, "end": v(3090, 1895) * mm});
            skPoint(sketch, "E39.4.3.2", {"position": v(3115, 1870) * mm});
            skLineSegment(sketch, "E39.4.3.3", {"start": v(3140, 1845) * mm, "end": v(3090, 1845) * mm});
            skLineSegment(sketch, "E39.4.3.4", {"start": v(3140, 1845) * mm, "end": v(3140, 1895) * mm});
            skLineSegment(sketch, "E39.4.4.0", {"start": v(3090, 1785) * mm, "end": v(3090, 1835) * mm});
            skLineSegment(sketch, "E39.4.4.1", {"start": v(3140, 1835) * mm, "end": v(3090, 1835) * mm});
            skPoint(sketch, "E39.4.4.2", {"position": v(3115, 1810) * mm});
            skLineSegment(sketch, "E39.4.4.3", {"start": v(3140, 1785) * mm, "end": v(3090, 1785) * mm});
            skLineSegment(sketch, "E39.4.4.4", {"start": v(3140, 1785) * mm, "end": v(3140, 1835) * mm});
            skLineSegment(sketch, "E39.4.5.0", {"start": v(3090, 1725) * mm, "end": v(3090, 1775) * mm});
            skLineSegment(sketch, "E39.4.5.1", {"start": v(3140, 1775) * mm, "end": v(3090, 1775) * mm});
            skPoint(sketch, "E39.4.5.2", {"position": v(3115, 1750) * mm});
            skLineSegment(sketch, "E39.4.5.3", {"start": v(3140, 1725) * mm, "end": v(3090, 1725) * mm});
            skLineSegment(sketch, "E39.4.5.4", {"start": v(3140, 1725) * mm, "end": v(3140, 1775) * mm});
            skLineSegment(sketch, "E39.4.6.0", {"start": v(3090, 1665) * mm, "end": v(3090, 1715) * mm});
            skLineSegment(sketch, "E39.4.6.1", {"start": v(3140, 1715) * mm, "end": v(3090, 1715) * mm});
            skPoint(sketch, "E39.4.6.2", {"position": v(3115, 1690) * mm});
            skLineSegment(sketch, "E39.4.6.3", {"start": v(3140, 1665) * mm, "end": v(3090, 1665) * mm});
            skLineSegment(sketch, "E39.4.6.4", {"start": v(3140, 1665) * mm, "end": v(3140, 1715) * mm});
            skLineSegment(sketch, "E39.4.7.0", {"start": v(3090, 1605) * mm, "end": v(3090, 1655) * mm});
            skLineSegment(sketch, "E39.4.7.1", {"start": v(3140, 1655) * mm, "end": v(3090, 1655) * mm});
            skPoint(sketch, "E39.4.7.2", {"position": v(3115, 1630) * mm});
            skLineSegment(sketch, "E39.4.7.3", {"start": v(3140, 1605) * mm, "end": v(3090, 1605) * mm});
            skLineSegment(sketch, "E39.4.7.4", {"start": v(3140, 1605) * mm, "end": v(3140, 1655) * mm});
            skLineSegment(sketch, "E39.4.8.0", {"start": v(3090, 1545) * mm, "end": v(3090, 1595) * mm});
            skLineSegment(sketch, "E39.4.8.1", {"start": v(3140, 1595) * mm, "end": v(3090, 1595) * mm});
            skPoint(sketch, "E39.4.8.2", {"position": v(3115, 1570) * mm});
            skLineSegment(sketch, "E39.4.8.3", {"start": v(3140, 1545) * mm, "end": v(3090, 1545) * mm});
            skLineSegment(sketch, "E39.4.8.4", {"start": v(3140, 1545) * mm, "end": v(3140, 1595) * mm});
            skLineSegment(sketch, "E39.4.9.0", {"start": v(3090, 1485) * mm, "end": v(3090, 1535) * mm});
            skLineSegment(sketch, "E39.4.9.1", {"start": v(3140, 1535) * mm, "end": v(3090, 1535) * mm});
            skPoint(sketch, "E39.4.9.2", {"position": v(3115, 1510) * mm});
            skLineSegment(sketch, "E39.4.9.3", {"start": v(3140, 1485) * mm, "end": v(3090, 1485) * mm});
            skLineSegment(sketch, "E39.4.9.4", {"start": v(3140, 1485) * mm, "end": v(3140, 1535) * mm});
            skLineSegment(sketch, "E39.4.10.0", {"start": v(3090, 1425) * mm, "end": v(3090, 1475) * mm});
            skLineSegment(sketch, "E39.4.10.1", {"start": v(3140, 1475) * mm, "end": v(3090, 1475) * mm});
            skPoint(sketch, "E39.4.10.2", {"position": v(3115, 1450) * mm});
            skLineSegment(sketch, "E39.4.10.3", {"start": v(3140, 1425) * mm, "end": v(3090, 1425) * mm});
            skLineSegment(sketch, "E39.4.10.4", {"start": v(3140, 1425) * mm, "end": v(3140, 1475) * mm});
            skLineSegment(sketch, "E39.4.11.0", {"start": v(3090, 1365) * mm, "end": v(3090, 1415) * mm});
            skLineSegment(sketch, "E39.4.11.1", {"start": v(3140, 1415) * mm, "end": v(3090, 1415) * mm});
            skPoint(sketch, "E39.4.11.2", {"position": v(3115, 1390) * mm});
            skLineSegment(sketch, "E39.4.11.3", {"start": v(3140, 1365) * mm, "end": v(3090, 1365) * mm});
            skLineSegment(sketch, "E39.4.11.4", {"start": v(3140, 1365) * mm, "end": v(3140, 1415) * mm});
            skLineSegment(sketch, "E39.5.0.0", {"start": v(3150, 2025) * mm, "end": v(3150, 2075) * mm});
            skLineSegment(sketch, "E39.5.0.1", {"start": v(3200, 2075) * mm, "end": v(3150, 2075) * mm});
            skPoint(sketch, "E39.5.0.2", {"position": v(3175, 2050) * mm});
            skLineSegment(sketch, "E39.5.0.3", {"start": v(3200, 2025) * mm, "end": v(3150, 2025) * mm});
            skLineSegment(sketch, "E39.5.0.4", {"start": v(3200, 2025) * mm, "end": v(3200, 2075) * mm});
            skLineSegment(sketch, "E39.5.1.0", {"start": v(3150, 1965) * mm, "end": v(3150, 2015) * mm});
            skLineSegment(sketch, "E39.5.1.1", {"start": v(3200, 2015) * mm, "end": v(3150, 2015) * mm});
            skPoint(sketch, "E39.5.1.2", {"position": v(3175, 1990) * mm});
            skLineSegment(sketch, "E39.5.1.3", {"start": v(3200, 1965) * mm, "end": v(3150, 1965) * mm});
            skLineSegment(sketch, "E39.5.1.4", {"start": v(3200, 1965) * mm, "end": v(3200, 2015) * mm});
            skLineSegment(sketch, "E39.5.2.0", {"start": v(3150, 1905) * mm, "end": v(3150, 1955) * mm});
            skLineSegment(sketch, "E39.5.2.1", {"start": v(3200, 1955) * mm, "end": v(3150, 1955) * mm});
            skPoint(sketch, "E39.5.2.2", {"position": v(3175, 1930) * mm});
            skLineSegment(sketch, "E39.5.2.3", {"start": v(3200, 1905) * mm, "end": v(3150, 1905) * mm});
            skLineSegment(sketch, "E39.5.2.4", {"start": v(3200, 1905) * mm, "end": v(3200, 1955) * mm});
            skLineSegment(sketch, "E39.5.3.0", {"start": v(3150, 1845) * mm, "end": v(3150, 1895) * mm});
            skLineSegment(sketch, "E39.5.3.1", {"start": v(3200, 1895) * mm, "end": v(3150, 1895) * mm});
            skPoint(sketch, "E39.5.3.2", {"position": v(3175, 1870) * mm});
            skLineSegment(sketch, "E39.5.3.3", {"start": v(3200, 1845) * mm, "end": v(3150, 1845) * mm});
            skLineSegment(sketch, "E39.5.3.4", {"start": v(3200, 1845) * mm, "end": v(3200, 1895) * mm});
            skLineSegment(sketch, "E39.5.4.0", {"start": v(3150, 1785) * mm, "end": v(3150, 1835) * mm});
            skLineSegment(sketch, "E39.5.4.1", {"start": v(3200, 1835) * mm, "end": v(3150, 1835) * mm});
            skPoint(sketch, "E39.5.4.2", {"position": v(3175, 1810) * mm});
            skLineSegment(sketch, "E39.5.4.3", {"start": v(3200, 1785) * mm, "end": v(3150, 1785) * mm});
            skLineSegment(sketch, "E39.5.4.4", {"start": v(3200, 1785) * mm, "end": v(3200, 1835) * mm});
            skLineSegment(sketch, "E39.5.5.0", {"start": v(3150, 1725) * mm, "end": v(3150, 1775) * mm});
            skLineSegment(sketch, "E39.5.5.1", {"start": v(3200, 1775) * mm, "end": v(3150, 1775) * mm});
            skPoint(sketch, "E39.5.5.2", {"position": v(3175, 1750) * mm});
            skLineSegment(sketch, "E39.5.5.3", {"start": v(3200, 1725) * mm, "end": v(3150, 1725) * mm});
            skLineSegment(sketch, "E39.5.5.4", {"start": v(3200, 1725) * mm, "end": v(3200, 1775) * mm});
            skLineSegment(sketch, "E39.5.6.0", {"start": v(3150, 1665) * mm, "end": v(3150, 1715) * mm});
            skLineSegment(sketch, "E39.5.6.1", {"start": v(3200, 1715) * mm, "end": v(3150, 1715) * mm});
            skPoint(sketch, "E39.5.6.2", {"position": v(3175, 1690) * mm});
            skLineSegment(sketch, "E39.5.6.3", {"start": v(3200, 1665) * mm, "end": v(3150, 1665) * mm});
            skLineSegment(sketch, "E39.5.6.4", {"start": v(3200, 1665) * mm, "end": v(3200, 1715) * mm});
            skLineSegment(sketch, "E39.5.7.0", {"start": v(3150, 1605) * mm, "end": v(3150, 1655) * mm});
            skLineSegment(sketch, "E39.5.7.1", {"start": v(3200, 1655) * mm, "end": v(3150, 1655) * mm});
            skPoint(sketch, "E39.5.7.2", {"position": v(3175, 1630) * mm});
            skLineSegment(sketch, "E39.5.7.3", {"start": v(3200, 1605) * mm, "end": v(3150, 1605) * mm});
            skLineSegment(sketch, "E39.5.7.4", {"start": v(3200, 1605) * mm, "end": v(3200, 1655) * mm});
            skLineSegment(sketch, "E39.5.8.0", {"start": v(3150, 1545) * mm, "end": v(3150, 1595) * mm});
            skLineSegment(sketch, "E39.5.8.1", {"start": v(3200, 1595) * mm, "end": v(3150, 1595) * mm});
            skPoint(sketch, "E39.5.8.2", {"position": v(3175, 1570) * mm});
            skLineSegment(sketch, "E39.5.8.3", {"start": v(3200, 1545) * mm, "end": v(3150, 1545) * mm});
            skLineSegment(sketch, "E39.5.8.4", {"start": v(3200, 1545) * mm, "end": v(3200, 1595) * mm});
            skLineSegment(sketch, "E39.5.9.0", {"start": v(3150, 1485) * mm, "end": v(3150, 1535) * mm});
            skLineSegment(sketch, "E39.5.9.1", {"start": v(3200, 1535) * mm, "end": v(3150, 1535) * mm});
            skPoint(sketch, "E39.5.9.2", {"position": v(3175, 1510) * mm});
            skLineSegment(sketch, "E39.5.9.3", {"start": v(3200, 1485) * mm, "end": v(3150, 1485) * mm});
            skLineSegment(sketch, "E39.5.9.4", {"start": v(3200, 1485) * mm, "end": v(3200, 1535) * mm});
            skLineSegment(sketch, "E39.5.10.0", {"start": v(3150, 1425) * mm, "end": v(3150, 1475) * mm});
            skLineSegment(sketch, "E39.5.10.1", {"start": v(3200, 1475) * mm, "end": v(3150, 1475) * mm});
            skPoint(sketch, "E39.5.10.2", {"position": v(3175, 1450) * mm});
            skLineSegment(sketch, "E39.5.10.3", {"start": v(3200, 1425) * mm, "end": v(3150, 1425) * mm});
            skLineSegment(sketch, "E39.5.10.4", {"start": v(3200, 1425) * mm, "end": v(3200, 1475) * mm});
            skLineSegment(sketch, "E39.5.11.0", {"start": v(3150, 1365) * mm, "end": v(3150, 1415) * mm});
            skLineSegment(sketch, "E39.5.11.1", {"start": v(3200, 1415) * mm, "end": v(3150, 1415) * mm});
            skPoint(sketch, "E39.5.11.2", {"position": v(3175, 1390) * mm});
            skLineSegment(sketch, "E39.5.11.3", {"start": v(3200, 1365) * mm, "end": v(3150, 1365) * mm});
            skLineSegment(sketch, "E39.5.11.4", {"start": v(3200, 1365) * mm, "end": v(3200, 1415) * mm});
            skLineSegment(sketch, "E39.6.0.0", {"start": v(3210, 2025) * mm, "end": v(3210, 2075) * mm});
            skLineSegment(sketch, "E39.6.0.1", {"start": v(3260, 2075) * mm, "end": v(3210, 2075) * mm});
            skPoint(sketch, "E39.6.0.2", {"position": v(3235, 2050) * mm});
            skLineSegment(sketch, "E39.6.0.3", {"start": v(3260, 2025) * mm, "end": v(3210, 2025) * mm});
            skLineSegment(sketch, "E39.6.0.4", {"start": v(3260, 2025) * mm, "end": v(3260, 2075) * mm});
            skLineSegment(sketch, "E39.6.1.0", {"start": v(3210, 1965) * mm, "end": v(3210, 2015) * mm});
            skLineSegment(sketch, "E39.6.1.1", {"start": v(3260, 2015) * mm, "end": v(3210, 2015) * mm});
            skPoint(sketch, "E39.6.1.2", {"position": v(3235, 1990) * mm});
            skLineSegment(sketch, "E39.6.1.3", {"start": v(3260, 1965) * mm, "end": v(3210, 1965) * mm});
            skLineSegment(sketch, "E39.6.1.4", {"start": v(3260, 1965) * mm, "end": v(3260, 2015) * mm});
            skLineSegment(sketch, "E39.6.2.0", {"start": v(3210, 1905) * mm, "end": v(3210, 1955) * mm});
            skLineSegment(sketch, "E39.6.2.1", {"start": v(3260, 1955) * mm, "end": v(3210, 1955) * mm});
            skPoint(sketch, "E39.6.2.2", {"position": v(3235, 1930) * mm});
            skLineSegment(sketch, "E39.6.2.3", {"start": v(3260, 1905) * mm, "end": v(3210, 1905) * mm});
            skLineSegment(sketch, "E39.6.2.4", {"start": v(3260, 1905) * mm, "end": v(3260, 1955) * mm});
            skLineSegment(sketch, "E39.6.3.0", {"start": v(3210, 1845) * mm, "end": v(3210, 1895) * mm});
            skLineSegment(sketch, "E39.6.3.1", {"start": v(3260, 1895) * mm, "end": v(3210, 1895) * mm});
            skPoint(sketch, "E39.6.3.2", {"position": v(3235, 1870) * mm});
            skLineSegment(sketch, "E39.6.3.3", {"start": v(3260, 1845) * mm, "end": v(3210, 1845) * mm});
            skLineSegment(sketch, "E39.6.3.4", {"start": v(3260, 1845) * mm, "end": v(3260, 1895) * mm});
            skLineSegment(sketch, "E39.6.4.0", {"start": v(3210, 1785) * mm, "end": v(3210, 1835) * mm});
            skLineSegment(sketch, "E39.6.4.1", {"start": v(3260, 1835) * mm, "end": v(3210, 1835) * mm});
            skPoint(sketch, "E39.6.4.2", {"position": v(3235, 1810) * mm});
            skLineSegment(sketch, "E39.6.4.3", {"start": v(3260, 1785) * mm, "end": v(3210, 1785) * mm});
            skLineSegment(sketch, "E39.6.4.4", {"start": v(3260, 1785) * mm, "end": v(3260, 1835) * mm});
            skLineSegment(sketch, "E39.6.5.0", {"start": v(3210, 1725) * mm, "end": v(3210, 1775) * mm});
            skLineSegment(sketch, "E39.6.5.1", {"start": v(3260, 1775) * mm, "end": v(3210, 1775) * mm});
            skPoint(sketch, "E39.6.5.2", {"position": v(3235, 1750) * mm});
            skLineSegment(sketch, "E39.6.5.3", {"start": v(3260, 1725) * mm, "end": v(3210, 1725) * mm});
            skLineSegment(sketch, "E39.6.5.4", {"start": v(3260, 1725) * mm, "end": v(3260, 1775) * mm});
            skLineSegment(sketch, "E39.6.6.0", {"start": v(3210, 1665) * mm, "end": v(3210, 1715) * mm});
            skLineSegment(sketch, "E39.6.6.1", {"start": v(3260, 1715) * mm, "end": v(3210, 1715) * mm});
            skPoint(sketch, "E39.6.6.2", {"position": v(3235, 1690) * mm});
            skLineSegment(sketch, "E39.6.6.3", {"start": v(3260, 1665) * mm, "end": v(3210, 1665) * mm});
            skLineSegment(sketch, "E39.6.6.4", {"start": v(3260, 1665) * mm, "end": v(3260, 1715) * mm});
            skLineSegment(sketch, "E39.6.7.0", {"start": v(3210, 1605) * mm, "end": v(3210, 1655) * mm});
            skLineSegment(sketch, "E39.6.7.1", {"start": v(3260, 1655) * mm, "end": v(3210, 1655) * mm});
            skPoint(sketch, "E39.6.7.2", {"position": v(3235, 1630) * mm});
            skLineSegment(sketch, "E39.6.7.3", {"start": v(3260, 1605) * mm, "end": v(3210, 1605) * mm});
            skLineSegment(sketch, "E39.6.7.4", {"start": v(3260, 1605) * mm, "end": v(3260, 1655) * mm});
            skLineSegment(sketch, "E39.6.8.0", {"start": v(3210, 1545) * mm, "end": v(3210, 1595) * mm});
            skLineSegment(sketch, "E39.6.8.1", {"start": v(3260, 1595) * mm, "end": v(3210, 1595) * mm});
            skPoint(sketch, "E39.6.8.2", {"position": v(3235, 1570) * mm});
            skLineSegment(sketch, "E39.6.8.3", {"start": v(3260, 1545) * mm, "end": v(3210, 1545) * mm});
            skLineSegment(sketch, "E39.6.8.4", {"start": v(3260, 1545) * mm, "end": v(3260, 1595) * mm});
            skLineSegment(sketch, "E39.6.9.0", {"start": v(3210, 1485) * mm, "end": v(3210, 1535) * mm});
            skLineSegment(sketch, "E39.6.9.1", {"start": v(3260, 1535) * mm, "end": v(3210, 1535) * mm});
            skPoint(sketch, "E39.6.9.2", {"position": v(3235, 1510) * mm});
            skLineSegment(sketch, "E39.6.9.3", {"start": v(3260, 1485) * mm, "end": v(3210, 1485) * mm});
            skLineSegment(sketch, "E39.6.9.4", {"start": v(3260, 1485) * mm, "end": v(3260, 1535) * mm});
            skLineSegment(sketch, "E39.6.10.0", {"start": v(3210, 1425) * mm, "end": v(3210, 1475) * mm});
            skLineSegment(sketch, "E39.6.10.1", {"start": v(3260, 1475) * mm, "end": v(3210, 1475) * mm});
            skPoint(sketch, "E39.6.10.2", {"position": v(3235, 1450) * mm});
            skLineSegment(sketch, "E39.6.10.3", {"start": v(3260, 1425) * mm, "end": v(3210, 1425) * mm});
            skLineSegment(sketch, "E39.6.10.4", {"start": v(3260, 1425) * mm, "end": v(3260, 1475) * mm});
            skLineSegment(sketch, "E39.6.11.0", {"start": v(3210, 1365) * mm, "end": v(3210, 1415) * mm});
            skLineSegment(sketch, "E39.6.11.1", {"start": v(3260, 1415) * mm, "end": v(3210, 1415) * mm});
            skPoint(sketch, "E39.6.11.2", {"position": v(3235, 1390) * mm});
            skLineSegment(sketch, "E39.6.11.3", {"start": v(3260, 1365) * mm, "end": v(3210, 1365) * mm});
            skLineSegment(sketch, "E39.6.11.4", {"start": v(3260, 1365) * mm, "end": v(3260, 1415) * mm});
            skLineSegment(sketch, "E39.7.0.0", {"start": v(3270, 2025) * mm, "end": v(3270, 2075) * mm});
            skLineSegment(sketch, "E39.7.0.1", {"start": v(3320, 2075) * mm, "end": v(3270, 2075) * mm});
            skPoint(sketch, "E39.7.0.2", {"position": v(3295, 2050) * mm});
            skLineSegment(sketch, "E39.7.0.3", {"start": v(3320, 2025) * mm, "end": v(3270, 2025) * mm});
            skLineSegment(sketch, "E39.7.0.4", {"start": v(3320, 2025) * mm, "end": v(3320, 2075) * mm});
            skLineSegment(sketch, "E39.7.1.0", {"start": v(3270, 1965) * mm, "end": v(3270, 2015) * mm});
            skLineSegment(sketch, "E39.7.1.1", {"start": v(3320, 2015) * mm, "end": v(3270, 2015) * mm});
            skPoint(sketch, "E39.7.1.2", {"position": v(3295, 1990) * mm});
            skLineSegment(sketch, "E39.7.1.3", {"start": v(3320, 1965) * mm, "end": v(3270, 1965) * mm});
            skLineSegment(sketch, "E39.7.1.4", {"start": v(3320, 1965) * mm, "end": v(3320, 2015) * mm});
            skLineSegment(sketch, "E39.7.2.0", {"start": v(3270, 1905) * mm, "end": v(3270, 1955) * mm});
            skLineSegment(sketch, "E39.7.2.1", {"start": v(3320, 1955) * mm, "end": v(3270, 1955) * mm});
            skPoint(sketch, "E39.7.2.2", {"position": v(3295, 1930) * mm});
            skLineSegment(sketch, "E39.7.2.3", {"start": v(3320, 1905) * mm, "end": v(3270, 1905) * mm});
            skLineSegment(sketch, "E39.7.2.4", {"start": v(3320, 1905) * mm, "end": v(3320, 1955) * mm});
            skLineSegment(sketch, "E39.7.3.0", {"start": v(3270, 1845) * mm, "end": v(3270, 1895) * mm});
            skLineSegment(sketch, "E39.7.3.1", {"start": v(3320, 1895) * mm, "end": v(3270, 1895) * mm});
            skPoint(sketch, "E39.7.3.2", {"position": v(3295, 1870) * mm});
            skLineSegment(sketch, "E39.7.3.3", {"start": v(3320, 1845) * mm, "end": v(3270, 1845) * mm});
            skLineSegment(sketch, "E39.7.3.4", {"start": v(3320, 1845) * mm, "end": v(3320, 1895) * mm});
            skLineSegment(sketch, "E39.7.4.0", {"start": v(3270, 1785) * mm, "end": v(3270, 1835) * mm});
            skLineSegment(sketch, "E39.7.4.1", {"start": v(3320, 1835) * mm, "end": v(3270, 1835) * mm});
            skPoint(sketch, "E39.7.4.2", {"position": v(3295, 1810) * mm});
            skLineSegment(sketch, "E39.7.4.3", {"start": v(3320, 1785) * mm, "end": v(3270, 1785) * mm});
            skLineSegment(sketch, "E39.7.4.4", {"start": v(3320, 1785) * mm, "end": v(3320, 1835) * mm});
            skLineSegment(sketch, "E39.7.5.0", {"start": v(3270, 1725) * mm, "end": v(3270, 1775) * mm});
            skLineSegment(sketch, "E39.7.5.1", {"start": v(3320, 1775) * mm, "end": v(3270, 1775) * mm});
            skPoint(sketch, "E39.7.5.2", {"position": v(3295, 1750) * mm});
            skLineSegment(sketch, "E39.7.5.3", {"start": v(3320, 1725) * mm, "end": v(3270, 1725) * mm});
            skLineSegment(sketch, "E39.7.5.4", {"start": v(3320, 1725) * mm, "end": v(3320, 1775) * mm});
            skLineSegment(sketch, "E39.7.6.0", {"start": v(3270, 1665) * mm, "end": v(3270, 1715) * mm});
            skLineSegment(sketch, "E39.7.6.1", {"start": v(3320, 1715) * mm, "end": v(3270, 1715) * mm});
            skPoint(sketch, "E39.7.6.2", {"position": v(3295, 1690) * mm});
            skLineSegment(sketch, "E39.7.6.3", {"start": v(3320, 1665) * mm, "end": v(3270, 1665) * mm});
            skLineSegment(sketch, "E39.7.6.4", {"start": v(3320, 1665) * mm, "end": v(3320, 1715) * mm});
            skLineSegment(sketch, "E39.7.7.0", {"start": v(3270, 1605) * mm, "end": v(3270, 1655) * mm});
            skLineSegment(sketch, "E39.7.7.1", {"start": v(3320, 1655) * mm, "end": v(3270, 1655) * mm});
            skPoint(sketch, "E39.7.7.2", {"position": v(3295, 1630) * mm});
            skLineSegment(sketch, "E39.7.7.3", {"start": v(3320, 1605) * mm, "end": v(3270, 1605) * mm});
            skLineSegment(sketch, "E39.7.7.4", {"start": v(3320, 1605) * mm, "end": v(3320, 1655) * mm});
            skLineSegment(sketch, "E39.7.8.0", {"start": v(3270, 1545) * mm, "end": v(3270, 1595) * mm});
            skLineSegment(sketch, "E39.7.8.1", {"start": v(3320, 1595) * mm, "end": v(3270, 1595) * mm});
            skPoint(sketch, "E39.7.8.2", {"position": v(3295, 1570) * mm});
            skLineSegment(sketch, "E39.7.8.3", {"start": v(3320, 1545) * mm, "end": v(3270, 1545) * mm});
            skLineSegment(sketch, "E39.7.8.4", {"start": v(3320, 1545) * mm, "end": v(3320, 1595) * mm});
            skLineSegment(sketch, "E39.7.9.0", {"start": v(3270, 1485) * mm, "end": v(3270, 1535) * mm});
            skLineSegment(sketch, "E39.7.9.1", {"start": v(3320, 1535) * mm, "end": v(3270, 1535) * mm});
            skPoint(sketch, "E39.7.9.2", {"position": v(3295, 1510) * mm});
            skLineSegment(sketch, "E39.7.9.3", {"start": v(3320, 1485) * mm, "end": v(3270, 1485) * mm});
            skLineSegment(sketch, "E39.7.9.4", {"start": v(3320, 1485) * mm, "end": v(3320, 1535) * mm});
            skLineSegment(sketch, "E39.7.10.0", {"start": v(3270, 1425) * mm, "end": v(3270, 1475) * mm});
            skLineSegment(sketch, "E39.7.10.1", {"start": v(3320, 1475) * mm, "end": v(3270, 1475) * mm});
            skPoint(sketch, "E39.7.10.2", {"position": v(3295, 1450) * mm});
            skLineSegment(sketch, "E39.7.10.3", {"start": v(3320, 1425) * mm, "end": v(3270, 1425) * mm});
            skLineSegment(sketch, "E39.7.10.4", {"start": v(3320, 1425) * mm, "end": v(3320, 1475) * mm});
            skLineSegment(sketch, "E39.7.11.0", {"start": v(3270, 1365) * mm, "end": v(3270, 1415) * mm});
            skLineSegment(sketch, "E39.7.11.1", {"start": v(3320, 1415) * mm, "end": v(3270, 1415) * mm});
            skPoint(sketch, "E39.7.11.2", {"position": v(3295, 1390) * mm});
            skLineSegment(sketch, "E39.7.11.3", {"start": v(3320, 1365) * mm, "end": v(3270, 1365) * mm});
            skLineSegment(sketch, "E39.7.11.4", {"start": v(3320, 1365) * mm, "end": v(3320, 1415) * mm});
            skLineSegment(sketch, "E39.8.0.0", {"start": v(3330, 2025) * mm, "end": v(3330, 2075) * mm});
            skLineSegment(sketch, "E39.8.0.1", {"start": v(3380, 2075) * mm, "end": v(3330, 2075) * mm});
            skPoint(sketch, "E39.8.0.2", {"position": v(3355, 2050) * mm});
            skLineSegment(sketch, "E39.8.0.3", {"start": v(3380, 2025) * mm, "end": v(3330, 2025) * mm});
            skLineSegment(sketch, "E39.8.0.4", {"start": v(3380, 2025) * mm, "end": v(3380, 2075) * mm});
            skLineSegment(sketch, "E39.8.1.0", {"start": v(3330, 1965) * mm, "end": v(3330, 2015) * mm});
            skLineSegment(sketch, "E39.8.1.1", {"start": v(3380, 2015) * mm, "end": v(3330, 2015) * mm});
            skPoint(sketch, "E39.8.1.2", {"position": v(3355, 1990) * mm});
            skLineSegment(sketch, "E39.8.1.3", {"start": v(3380, 1965) * mm, "end": v(3330, 1965) * mm});
            skLineSegment(sketch, "E39.8.1.4", {"start": v(3380, 1965) * mm, "end": v(3380, 2015) * mm});
            skLineSegment(sketch, "E39.8.2.0", {"start": v(3330, 1905) * mm, "end": v(3330, 1955) * mm});
            skLineSegment(sketch, "E39.8.2.1", {"start": v(3380, 1955) * mm, "end": v(3330, 1955) * mm});
            skPoint(sketch, "E39.8.2.2", {"position": v(3355, 1930) * mm});
            skLineSegment(sketch, "E39.8.2.3", {"start": v(3380, 1905) * mm, "end": v(3330, 1905) * mm});
            skLineSegment(sketch, "E39.8.2.4", {"start": v(3380, 1905) * mm, "end": v(3380, 1955) * mm});
            skLineSegment(sketch, "E39.8.3.0", {"start": v(3330, 1845) * mm, "end": v(3330, 1895) * mm});
            skLineSegment(sketch, "E39.8.3.1", {"start": v(3380, 1895) * mm, "end": v(3330, 1895) * mm});
            skPoint(sketch, "E39.8.3.2", {"position": v(3355, 1870) * mm});
            skLineSegment(sketch, "E39.8.3.3", {"start": v(3380, 1845) * mm, "end": v(3330, 1845) * mm});
            skLineSegment(sketch, "E39.8.3.4", {"start": v(3380, 1845) * mm, "end": v(3380, 1895) * mm});
            skLineSegment(sketch, "E39.8.4.0", {"start": v(3330, 1785) * mm, "end": v(3330, 1835) * mm});
            skLineSegment(sketch, "E39.8.4.1", {"start": v(3380, 1835) * mm, "end": v(3330, 1835) * mm});
            skPoint(sketch, "E39.8.4.2", {"position": v(3355, 1810) * mm});
            skLineSegment(sketch, "E39.8.4.3", {"start": v(3380, 1785) * mm, "end": v(3330, 1785) * mm});
            skLineSegment(sketch, "E39.8.4.4", {"start": v(3380, 1785) * mm, "end": v(3380, 1835) * mm});
            skLineSegment(sketch, "E39.8.5.0", {"start": v(3330, 1725) * mm, "end": v(3330, 1775) * mm});
            skLineSegment(sketch, "E39.8.5.1", {"start": v(3380, 1775) * mm, "end": v(3330, 1775) * mm});
            skPoint(sketch, "E39.8.5.2", {"position": v(3355, 1750) * mm});
            skLineSegment(sketch, "E39.8.5.3", {"start": v(3380, 1725) * mm, "end": v(3330, 1725) * mm});
            skLineSegment(sketch, "E39.8.5.4", {"start": v(3380, 1725) * mm, "end": v(3380, 1775) * mm});
            skLineSegment(sketch, "E39.8.6.0", {"start": v(3330, 1665) * mm, "end": v(3330, 1715) * mm});
            skLineSegment(sketch, "E39.8.6.1", {"start": v(3380, 1715) * mm, "end": v(3330, 1715) * mm});
            skPoint(sketch, "E39.8.6.2", {"position": v(3355, 1690) * mm});
            skLineSegment(sketch, "E39.8.6.3", {"start": v(3380, 1665) * mm, "end": v(3330, 1665) * mm});
            skLineSegment(sketch, "E39.8.6.4", {"start": v(3380, 1665) * mm, "end": v(3380, 1715) * mm});
            skLineSegment(sketch, "E39.8.7.0", {"start": v(3330, 1605) * mm, "end": v(3330, 1655) * mm});
            skLineSegment(sketch, "E39.8.7.1", {"start": v(3380, 1655) * mm, "end": v(3330, 1655) * mm});
            skPoint(sketch, "E39.8.7.2", {"position": v(3355, 1630) * mm});
            skLineSegment(sketch, "E39.8.7.3", {"start": v(3380, 1605) * mm, "end": v(3330, 1605) * mm});
            skLineSegment(sketch, "E39.8.7.4", {"start": v(3380, 1605) * mm, "end": v(3380, 1655) * mm});
            skLineSegment(sketch, "E39.8.8.0", {"start": v(3330, 1545) * mm, "end": v(3330, 1595) * mm});
            skLineSegment(sketch, "E39.8.8.1", {"start": v(3380, 1595) * mm, "end": v(3330, 1595) * mm});
            skPoint(sketch, "E39.8.8.2", {"position": v(3355, 1570) * mm});
            skLineSegment(sketch, "E39.8.8.3", {"start": v(3380, 1545) * mm, "end": v(3330, 1545) * mm});
            skLineSegment(sketch, "E39.8.8.4", {"start": v(3380, 1545) * mm, "end": v(3380, 1595) * mm});
            skLineSegment(sketch, "E39.8.9.0", {"start": v(3330, 1485) * mm, "end": v(3330, 1535) * mm});
            skLineSegment(sketch, "E39.8.9.1", {"start": v(3380, 1535) * mm, "end": v(3330, 1535) * mm});
            skPoint(sketch, "E39.8.9.2", {"position": v(3355, 1510) * mm});
            skLineSegment(sketch, "E39.8.9.3", {"start": v(3380, 1485) * mm, "end": v(3330, 1485) * mm});
            skLineSegment(sketch, "E39.8.9.4", {"start": v(3380, 1485) * mm, "end": v(3380, 1535) * mm});
            skLineSegment(sketch, "E39.8.10.0", {"start": v(3330, 1425) * mm, "end": v(3330, 1475) * mm});
            skLineSegment(sketch, "E39.8.10.1", {"start": v(3380, 1475) * mm, "end": v(3330, 1475) * mm});
            skPoint(sketch, "E39.8.10.2", {"position": v(3355, 1450) * mm});
            skLineSegment(sketch, "E39.8.10.3", {"start": v(3380, 1425) * mm, "end": v(3330, 1425) * mm});
            skLineSegment(sketch, "E39.8.10.4", {"start": v(3380, 1425) * mm, "end": v(3380, 1475) * mm});
            skLineSegment(sketch, "E39.8.11.0", {"start": v(3330, 1365) * mm, "end": v(3330, 1415) * mm});
            skLineSegment(sketch, "E39.8.11.1", {"start": v(3380, 1415) * mm, "end": v(3330, 1415) * mm});
            skPoint(sketch, "E39.8.11.2", {"position": v(3355, 1390) * mm});
            skLineSegment(sketch, "E39.8.11.3", {"start": v(3380, 1365) * mm, "end": v(3330, 1365) * mm});
            skLineSegment(sketch, "E39.8.11.4", {"start": v(3380, 1365) * mm, "end": v(3380, 1415) * mm});
            skLineSegment(sketch, "E39.9.0.0", {"start": v(3390, 2025) * mm, "end": v(3390, 2075) * mm});
            skLineSegment(sketch, "E39.9.0.1", {"start": v(3440, 2075) * mm, "end": v(3390, 2075) * mm});
            skPoint(sketch, "E39.9.0.2", {"position": v(3415, 2050) * mm});
            skLineSegment(sketch, "E39.9.0.3", {"start": v(3440, 2025) * mm, "end": v(3390, 2025) * mm});
            skLineSegment(sketch, "E39.9.0.4", {"start": v(3440, 2025) * mm, "end": v(3440, 2075) * mm});
            skLineSegment(sketch, "E39.9.1.0", {"start": v(3390, 1965) * mm, "end": v(3390, 2015) * mm});
            skLineSegment(sketch, "E39.9.1.1", {"start": v(3440, 2015) * mm, "end": v(3390, 2015) * mm});
            skPoint(sketch, "E39.9.1.2", {"position": v(3415, 1990) * mm});
            skLineSegment(sketch, "E39.9.1.3", {"start": v(3440, 1965) * mm, "end": v(3390, 1965) * mm});
            skLineSegment(sketch, "E39.9.1.4", {"start": v(3440, 1965) * mm, "end": v(3440, 2015) * mm});
            skLineSegment(sketch, "E39.9.2.0", {"start": v(3390, 1905) * mm, "end": v(3390, 1955) * mm});
            skLineSegment(sketch, "E39.9.2.1", {"start": v(3440, 1955) * mm, "end": v(3390, 1955) * mm});
            skPoint(sketch, "E39.9.2.2", {"position": v(3415, 1930) * mm});
            skLineSegment(sketch, "E39.9.2.3", {"start": v(3440, 1905) * mm, "end": v(3390, 1905) * mm});
            skLineSegment(sketch, "E39.9.2.4", {"start": v(3440, 1905) * mm, "end": v(3440, 1955) * mm});
            skLineSegment(sketch, "E39.9.3.0", {"start": v(3390, 1845) * mm, "end": v(3390, 1895) * mm});
            skLineSegment(sketch, "E39.9.3.1", {"start": v(3440, 1895) * mm, "end": v(3390, 1895) * mm});
            skPoint(sketch, "E39.9.3.2", {"position": v(3415, 1870) * mm});
            skLineSegment(sketch, "E39.9.3.3", {"start": v(3440, 1845) * mm, "end": v(3390, 1845) * mm});
            skLineSegment(sketch, "E39.9.3.4", {"start": v(3440, 1845) * mm, "end": v(3440, 1895) * mm});
            skLineSegment(sketch, "E39.9.4.0", {"start": v(3390, 1785) * mm, "end": v(3390, 1835) * mm});
            skLineSegment(sketch, "E39.9.4.1", {"start": v(3440, 1835) * mm, "end": v(3390, 1835) * mm});
            skPoint(sketch, "E39.9.4.2", {"position": v(3415, 1810) * mm});
            skLineSegment(sketch, "E39.9.4.3", {"start": v(3440, 1785) * mm, "end": v(3390, 1785) * mm});
            skLineSegment(sketch, "E39.9.4.4", {"start": v(3440, 1785) * mm, "end": v(3440, 1835) * mm});
            skLineSegment(sketch, "E39.9.5.0", {"start": v(3390, 1725) * mm, "end": v(3390, 1775) * mm});
            skLineSegment(sketch, "E39.9.5.1", {"start": v(3440, 1775) * mm, "end": v(3390, 1775) * mm});
            skPoint(sketch, "E39.9.5.2", {"position": v(3415, 1750) * mm});
            skLineSegment(sketch, "E39.9.5.3", {"start": v(3440, 1725) * mm, "end": v(3390, 1725) * mm});
            skLineSegment(sketch, "E39.9.5.4", {"start": v(3440, 1725) * mm, "end": v(3440, 1775) * mm});
            skLineSegment(sketch, "E39.9.6.0", {"start": v(3390, 1665) * mm, "end": v(3390, 1715) * mm});
            skLineSegment(sketch, "E39.9.6.1", {"start": v(3440, 1715) * mm, "end": v(3390, 1715) * mm});
            skPoint(sketch, "E39.9.6.2", {"position": v(3415, 1690) * mm});
            skLineSegment(sketch, "E39.9.6.3", {"start": v(3440, 1665) * mm, "end": v(3390, 1665) * mm});
            skLineSegment(sketch, "E39.9.6.4", {"start": v(3440, 1665) * mm, "end": v(3440, 1715) * mm});
            skLineSegment(sketch, "E39.9.7.0", {"start": v(3390, 1605) * mm, "end": v(3390, 1655) * mm});
            skLineSegment(sketch, "E39.9.7.1", {"start": v(3440, 1655) * mm, "end": v(3390, 1655) * mm});
            skPoint(sketch, "E39.9.7.2", {"position": v(3415, 1630) * mm});
            skLineSegment(sketch, "E39.9.7.3", {"start": v(3440, 1605) * mm, "end": v(3390, 1605) * mm});
            skLineSegment(sketch, "E39.9.7.4", {"start": v(3440, 1605) * mm, "end": v(3440, 1655) * mm});
            skLineSegment(sketch, "E39.9.8.0", {"start": v(3390, 1545) * mm, "end": v(3390, 1595) * mm});
            skLineSegment(sketch, "E39.9.8.1", {"start": v(3440, 1595) * mm, "end": v(3390, 1595) * mm});
            skPoint(sketch, "E39.9.8.2", {"position": v(3415, 1570) * mm});
            skLineSegment(sketch, "E39.9.8.3", {"start": v(3440, 1545) * mm, "end": v(3390, 1545) * mm});
            skLineSegment(sketch, "E39.9.8.4", {"start": v(3440, 1545) * mm, "end": v(3440, 1595) * mm});
            skLineSegment(sketch, "E39.9.9.0", {"start": v(3390, 1485) * mm, "end": v(3390, 1535) * mm});
            skLineSegment(sketch, "E39.9.9.1", {"start": v(3440, 1535) * mm, "end": v(3390, 1535) * mm});
            skPoint(sketch, "E39.9.9.2", {"position": v(3415, 1510) * mm});
            skLineSegment(sketch, "E39.9.9.3", {"start": v(3440, 1485) * mm, "end": v(3390, 1485) * mm});
            skLineSegment(sketch, "E39.9.9.4", {"start": v(3440, 1485) * mm, "end": v(3440, 1535) * mm});
            skLineSegment(sketch, "E39.9.10.0", {"start": v(3390, 1425) * mm, "end": v(3390, 1475) * mm});
            skLineSegment(sketch, "E39.9.10.1", {"start": v(3440, 1475) * mm, "end": v(3390, 1475) * mm});
            skPoint(sketch, "E39.9.10.2", {"position": v(3415, 1450) * mm});
            skLineSegment(sketch, "E39.9.10.3", {"start": v(3440, 1425) * mm, "end": v(3390, 1425) * mm});
            skLineSegment(sketch, "E39.9.10.4", {"start": v(3440, 1425) * mm, "end": v(3440, 1475) * mm});
            skLineSegment(sketch, "E39.9.11.0", {"start": v(3390, 1365) * mm, "end": v(3390, 1415) * mm});
            skLineSegment(sketch, "E39.9.11.1", {"start": v(3440, 1415) * mm, "end": v(3390, 1415) * mm});
            skPoint(sketch, "E39.9.11.2", {"position": v(3415, 1390) * mm});
            skLineSegment(sketch, "E39.9.11.3", {"start": v(3440, 1365) * mm, "end": v(3390, 1365) * mm});
            skLineSegment(sketch, "E39.9.11.4", {"start": v(3440, 1365) * mm, "end": v(3440, 1415) * mm});
            skLineSegment(sketch, "E39.10.0.0", {"start": v(3450, 2025) * mm, "end": v(3450, 2075) * mm});
            skLineSegment(sketch, "E39.10.0.1", {"start": v(3500, 2075) * mm, "end": v(3450, 2075) * mm});
            skPoint(sketch, "E39.10.0.2", {"position": v(3475, 2050) * mm});
            skLineSegment(sketch, "E39.10.0.3", {"start": v(3500, 2025) * mm, "end": v(3450, 2025) * mm});
            skLineSegment(sketch, "E39.10.0.4", {"start": v(3500, 2025) * mm, "end": v(3500, 2075) * mm});
            skLineSegment(sketch, "E39.10.1.0", {"start": v(3450, 1965) * mm, "end": v(3450, 2015) * mm});
            skLineSegment(sketch, "E39.10.1.1", {"start": v(3500, 2015) * mm, "end": v(3450, 2015) * mm});
            skPoint(sketch, "E39.10.1.2", {"position": v(3475, 1990) * mm});
            skLineSegment(sketch, "E39.10.1.3", {"start": v(3500, 1965) * mm, "end": v(3450, 1965) * mm});
            skLineSegment(sketch, "E39.10.1.4", {"start": v(3500, 1965) * mm, "end": v(3500, 2015) * mm});
            skLineSegment(sketch, "E39.10.2.0", {"start": v(3450, 1905) * mm, "end": v(3450, 1955) * mm});
            skLineSegment(sketch, "E39.10.2.1", {"start": v(3500, 1955) * mm, "end": v(3450, 1955) * mm});
            skPoint(sketch, "E39.10.2.2", {"position": v(3475, 1930) * mm});
            skLineSegment(sketch, "E39.10.2.3", {"start": v(3500, 1905) * mm, "end": v(3450, 1905) * mm});
            skLineSegment(sketch, "E39.10.2.4", {"start": v(3500, 1905) * mm, "end": v(3500, 1955) * mm});
            skLineSegment(sketch, "E39.10.3.0", {"start": v(3450, 1845) * mm, "end": v(3450, 1895) * mm});
            skLineSegment(sketch, "E39.10.3.1", {"start": v(3500, 1895) * mm, "end": v(3450, 1895) * mm});
            skPoint(sketch, "E39.10.3.2", {"position": v(3475, 1870) * mm});
            skLineSegment(sketch, "E39.10.3.3", {"start": v(3500, 1845) * mm, "end": v(3450, 1845) * mm});
            skLineSegment(sketch, "E39.10.3.4", {"start": v(3500, 1845) * mm, "end": v(3500, 1895) * mm});
            skLineSegment(sketch, "E39.10.4.0", {"start": v(3450, 1785) * mm, "end": v(3450, 1835) * mm});
            skLineSegment(sketch, "E39.10.4.1", {"start": v(3500, 1835) * mm, "end": v(3450, 1835) * mm});
            skPoint(sketch, "E39.10.4.2", {"position": v(3475, 1810) * mm});
            skLineSegment(sketch, "E39.10.4.3", {"start": v(3500, 1785) * mm, "end": v(3450, 1785) * mm});
            skLineSegment(sketch, "E39.10.4.4", {"start": v(3500, 1785) * mm, "end": v(3500, 1835) * mm});
            skLineSegment(sketch, "E39.10.5.0", {"start": v(3450, 1725) * mm, "end": v(3450, 1775) * mm});
            skLineSegment(sketch, "E39.10.5.1", {"start": v(3500, 1775) * mm, "end": v(3450, 1775) * mm});
            skPoint(sketch, "E39.10.5.2", {"position": v(3475, 1750) * mm});
            skLineSegment(sketch, "E39.10.5.3", {"start": v(3500, 1725) * mm, "end": v(3450, 1725) * mm});
            skLineSegment(sketch, "E39.10.5.4", {"start": v(3500, 1725) * mm, "end": v(3500, 1775) * mm});
            skLineSegment(sketch, "E39.10.6.0", {"start": v(3450, 1665) * mm, "end": v(3450, 1715) * mm});
            skLineSegment(sketch, "E39.10.6.1", {"start": v(3500, 1715) * mm, "end": v(3450, 1715) * mm});
            skPoint(sketch, "E39.10.6.2", {"position": v(3475, 1690) * mm});
            skLineSegment(sketch, "E39.10.6.3", {"start": v(3500, 1665) * mm, "end": v(3450, 1665) * mm});
            skLineSegment(sketch, "E39.10.6.4", {"start": v(3500, 1665) * mm, "end": v(3500, 1715) * mm});
            skLineSegment(sketch, "E39.10.7.0", {"start": v(3450, 1605) * mm, "end": v(3450, 1655) * mm});
            skLineSegment(sketch, "E39.10.7.1", {"start": v(3500, 1655) * mm, "end": v(3450, 1655) * mm});
            skPoint(sketch, "E39.10.7.2", {"position": v(3475, 1630) * mm});
            skLineSegment(sketch, "E39.10.7.3", {"start": v(3500, 1605) * mm, "end": v(3450, 1605) * mm});
            skLineSegment(sketch, "E39.10.7.4", {"start": v(3500, 1605) * mm, "end": v(3500, 1655) * mm});
            skLineSegment(sketch, "E39.10.8.0", {"start": v(3450, 1545) * mm, "end": v(3450, 1595) * mm});
            skLineSegment(sketch, "E39.10.8.1", {"start": v(3500, 1595) * mm, "end": v(3450, 1595) * mm});
            skPoint(sketch, "E39.10.8.2", {"position": v(3475, 1570) * mm});
            skLineSegment(sketch, "E39.10.8.3", {"start": v(3500, 1545) * mm, "end": v(3450, 1545) * mm});
            skLineSegment(sketch, "E39.10.8.4", {"start": v(3500, 1545) * mm, "end": v(3500, 1595) * mm});
            skLineSegment(sketch, "E39.10.9.0", {"start": v(3450, 1485) * mm, "end": v(3450, 1535) * mm});
            skLineSegment(sketch, "E39.10.9.1", {"start": v(3500, 1535) * mm, "end": v(3450, 1535) * mm});
            skPoint(sketch, "E39.10.9.2", {"position": v(3475, 1510) * mm});
            skLineSegment(sketch, "E39.10.9.3", {"start": v(3500, 1485) * mm, "end": v(3450, 1485) * mm});
            skLineSegment(sketch, "E39.10.9.4", {"start": v(3500, 1485) * mm, "end": v(3500, 1535) * mm});
            skLineSegment(sketch, "E39.10.10.0", {"start": v(3450, 1425) * mm, "end": v(3450, 1475) * mm});
            skLineSegment(sketch, "E39.10.10.1", {"start": v(3500, 1475) * mm, "end": v(3450, 1475) * mm});
            skPoint(sketch, "E39.10.10.2", {"position": v(3475, 1450) * mm});
            skLineSegment(sketch, "E39.10.10.3", {"start": v(3500, 1425) * mm, "end": v(3450, 1425) * mm});
            skLineSegment(sketch, "E39.10.10.4", {"start": v(3500, 1425) * mm, "end": v(3500, 1475) * mm});
            skLineSegment(sketch, "E39.10.11.0", {"start": v(3450, 1365) * mm, "end": v(3450, 1415) * mm});
            skLineSegment(sketch, "E39.10.11.1", {"start": v(3500, 1415) * mm, "end": v(3450, 1415) * mm});
            skPoint(sketch, "E39.10.11.2", {"position": v(3475, 1390) * mm});
            skLineSegment(sketch, "E39.10.11.3", {"start": v(3500, 1365) * mm, "end": v(3450, 1365) * mm});
            skLineSegment(sketch, "E39.10.11.4", {"start": v(3500, 1365) * mm, "end": v(3500, 1415) * mm});
            skLineSegment(sketch, "E39.11.0.0", {"start": v(3510, 2025) * mm, "end": v(3510, 2075) * mm});
            skLineSegment(sketch, "E39.11.0.1", {"start": v(3560, 2075) * mm, "end": v(3510, 2075) * mm});
            skPoint(sketch, "E39.11.0.2", {"position": v(3535, 2050) * mm});
            skLineSegment(sketch, "E39.11.0.3", {"start": v(3560, 2025) * mm, "end": v(3510, 2025) * mm});
            skLineSegment(sketch, "E39.11.0.4", {"start": v(3560, 2025) * mm, "end": v(3560, 2075) * mm});
            skLineSegment(sketch, "E39.11.1.0", {"start": v(3510, 1965) * mm, "end": v(3510, 2015) * mm});
            skLineSegment(sketch, "E39.11.1.1", {"start": v(3560, 2015) * mm, "end": v(3510, 2015) * mm});
            skPoint(sketch, "E39.11.1.2", {"position": v(3535, 1990) * mm});
            skLineSegment(sketch, "E39.11.1.3", {"start": v(3560, 1965) * mm, "end": v(3510, 1965) * mm});
            skLineSegment(sketch, "E39.11.1.4", {"start": v(3560, 1965) * mm, "end": v(3560, 2015) * mm});
            skLineSegment(sketch, "E39.11.2.0", {"start": v(3510, 1905) * mm, "end": v(3510, 1955) * mm});
            skLineSegment(sketch, "E39.11.2.1", {"start": v(3560, 1955) * mm, "end": v(3510, 1955) * mm});
            skPoint(sketch, "E39.11.2.2", {"position": v(3535, 1930) * mm});
            skLineSegment(sketch, "E39.11.2.3", {"start": v(3560, 1905) * mm, "end": v(3510, 1905) * mm});
            skLineSegment(sketch, "E39.11.2.4", {"start": v(3560, 1905) * mm, "end": v(3560, 1955) * mm});
            skLineSegment(sketch, "E39.11.3.0", {"start": v(3510, 1845) * mm, "end": v(3510, 1895) * mm});
            skLineSegment(sketch, "E39.11.3.1", {"start": v(3560, 1895) * mm, "end": v(3510, 1895) * mm});
            skPoint(sketch, "E39.11.3.2", {"position": v(3535, 1870) * mm});
            skLineSegment(sketch, "E39.11.3.3", {"start": v(3560, 1845) * mm, "end": v(3510, 1845) * mm});
            skLineSegment(sketch, "E39.11.3.4", {"start": v(3560, 1845) * mm, "end": v(3560, 1895) * mm});
            skLineSegment(sketch, "E39.11.4.0", {"start": v(3510, 1785) * mm, "end": v(3510, 1835) * mm});
            skLineSegment(sketch, "E39.11.4.1", {"start": v(3560, 1835) * mm, "end": v(3510, 1835) * mm});
            skPoint(sketch, "E39.11.4.2", {"position": v(3535, 1810) * mm});
            skLineSegment(sketch, "E39.11.4.3", {"start": v(3560, 1785) * mm, "end": v(3510, 1785) * mm});
            skLineSegment(sketch, "E39.11.4.4", {"start": v(3560, 1785) * mm, "end": v(3560, 1835) * mm});
            skLineSegment(sketch, "E39.11.5.0", {"start": v(3510, 1725) * mm, "end": v(3510, 1775) * mm});
            skLineSegment(sketch, "E39.11.5.1", {"start": v(3560, 1775) * mm, "end": v(3510, 1775) * mm});
            skPoint(sketch, "E39.11.5.2", {"position": v(3535, 1750) * mm});
            skLineSegment(sketch, "E39.11.5.3", {"start": v(3560, 1725) * mm, "end": v(3510, 1725) * mm});
            skLineSegment(sketch, "E39.11.5.4", {"start": v(3560, 1725) * mm, "end": v(3560, 1775) * mm});
            skLineSegment(sketch, "E39.11.6.0", {"start": v(3510, 1665) * mm, "end": v(3510, 1715) * mm});
            skLineSegment(sketch, "E39.11.6.1", {"start": v(3560, 1715) * mm, "end": v(3510, 1715) * mm});
            skPoint(sketch, "E39.11.6.2", {"position": v(3535, 1690) * mm});
            skLineSegment(sketch, "E39.11.6.3", {"start": v(3560, 1665) * mm, "end": v(3510, 1665) * mm});
            skLineSegment(sketch, "E39.11.6.4", {"start": v(3560, 1665) * mm, "end": v(3560, 1715) * mm});
            skLineSegment(sketch, "E39.11.7.0", {"start": v(3510, 1605) * mm, "end": v(3510, 1655) * mm});
            skLineSegment(sketch, "E39.11.7.1", {"start": v(3560, 1655) * mm, "end": v(3510, 1655) * mm});
            skPoint(sketch, "E39.11.7.2", {"position": v(3535, 1630) * mm});
            skLineSegment(sketch, "E39.11.7.3", {"start": v(3560, 1605) * mm, "end": v(3510, 1605) * mm});
            skLineSegment(sketch, "E39.11.7.4", {"start": v(3560, 1605) * mm, "end": v(3560, 1655) * mm});
            skLineSegment(sketch, "E39.11.8.0", {"start": v(3510, 1545) * mm, "end": v(3510, 1595) * mm});
            skLineSegment(sketch, "E39.11.8.1", {"start": v(3560, 1595) * mm, "end": v(3510, 1595) * mm});
            skPoint(sketch, "E39.11.8.2", {"position": v(3535, 1570) * mm});
            skLineSegment(sketch, "E39.11.8.3", {"start": v(3560, 1545) * mm, "end": v(3510, 1545) * mm});
            skLineSegment(sketch, "E39.11.8.4", {"start": v(3560, 1545) * mm, "end": v(3560, 1595) * mm});
            skLineSegment(sketch, "E39.11.9.0", {"start": v(3510, 1485) * mm, "end": v(3510, 1535) * mm});
            skLineSegment(sketch, "E39.11.9.1", {"start": v(3560, 1535) * mm, "end": v(3510, 1535) * mm});
            skPoint(sketch, "E39.11.9.2", {"position": v(3535, 1510) * mm});
            skLineSegment(sketch, "E39.11.9.3", {"start": v(3560, 1485) * mm, "end": v(3510, 1485) * mm});
            skLineSegment(sketch, "E39.11.9.4", {"start": v(3560, 1485) * mm, "end": v(3560, 1535) * mm});
            skLineSegment(sketch, "E39.11.10.0", {"start": v(3510, 1425) * mm, "end": v(3510, 1475) * mm});
            skLineSegment(sketch, "E39.11.10.1", {"start": v(3560, 1475) * mm, "end": v(3510, 1475) * mm});
            skPoint(sketch, "E39.11.10.2", {"position": v(3535, 1450) * mm});
            skLineSegment(sketch, "E39.11.10.3", {"start": v(3560, 1425) * mm, "end": v(3510, 1425) * mm});
            skLineSegment(sketch, "E39.11.10.4", {"start": v(3560, 1425) * mm, "end": v(3560, 1475) * mm});
            skLineSegment(sketch, "E39.11.11.0", {"start": v(3510, 1365) * mm, "end": v(3510, 1415) * mm});
            skLineSegment(sketch, "E39.11.11.1", {"start": v(3560, 1415) * mm, "end": v(3510, 1415) * mm});
            skPoint(sketch, "E39.11.11.2", {"position": v(3535, 1390) * mm});
            skLineSegment(sketch, "E39.11.11.3", {"start": v(3560, 1365) * mm, "end": v(3510, 1365) * mm});
            skLineSegment(sketch, "E39.11.11.4", {"start": v(3560, 1365) * mm, "end": v(3560, 1415) * mm});
            skLineSegment(sketch, "E39.direction1", {"start": v(2850, 2025) * mm, "end": v(2910, 2025) * mm, "construction": true});
            skLineSegment(sketch, "E39.direction2", {"start": v(2850, 2025) * mm, "end": v(2850, 1965) * mm, "construction": true});
            skPoint(sketch, "E37.left.end.orphan", {"position": v(3600, 2125) * mm});
            skPoint(sketch, "E37.bottom.start.orphan", {"position": v(3600, 1325) * mm});
            skPoint(sketch, "E37.right.end.orphan", {"position": v(2800, 2125) * mm});
            skPoint(sketch, "E37.right.start.orphan", {"position": v(2800, 1325) * mm});
            skSolve(sketch);
        }
        {
            var Q0;
            Q0 = qSketchRegion(id + "F23", true);
            extrude(context, id + "F24", {"entities" : qUnion([Q0]), "operationType" : NewBodyOperationType.REMOVE, "oppositeDirection" : true, "depth" : 50 * mm, "offsetDistance" : 25 * mm});
        }
        {
            var Q0;
            Q0=makeQuery(id+"F1.opExtrude","CAP_FACE",FACE,{"disambiguationData":[OSD([sQuery(id+"F0.wireOp",EDGE,"E0.bottom"),sQuery(id+"F0.wireOp",EDGE,"E0.top"),sQuery(id+"F0.wireOp",EDGE,"E0.left"),sQuery(id+"F0.wireOp",EDGE,"E0.right")])],"isStart":true});
            extrude(context, id + "F25", {"entities" : qUnion([Q0]), "operationType" : NewBodyOperationType.ADD, "depth" : (140 - 25) * mm, "offsetDistance" : 25 * mm});
        }
        {
            var Q0;
            Q0=makeQuery(id+"F9.opExtrude","SWEPT_FACE",FACE,{"disambiguationData":[OSD([sQuery(id+"F8.wireOp",EDGE,"E15.bottom")])]});
            var sketch = newSketch(context, id + "F26", { "sketchPlane" : qUnion([Q0])});
            skCircle(sketch, "E40", {"center": v(2550, -1220.07) * mm, "radius": 5 * mm});
            skCircle(sketch, "E41.1.0.0", {"center": v(1050, -1220.07) * mm, "radius": 5 * mm});
            skCircle(sketch, "E41.2.0.0", {"center": v(-450, -1220.07) * mm, "radius": 5 * mm});
            skCircle(sketch, "E41.3.0.0", {"center": v(-1950, -1220.07) * mm, "radius": 5 * mm});
            skLineSegment(sketch, "E41.direction1", {"start": v(2550, -1220.07) * mm, "end": v(1050, -1220.07) * mm, "construction": true});
            skSolve(sketch);
        }
        {
            var Q0;
            Q0 = qSketchRegion(id + "F26", true);
            extrude(context, id + "F27", {"entities" : qUnion([Q0]), "operationType" : NewBodyOperationType.ADD, "depth" : 900 * mm, "offsetDistance" : 25 * mm, "hasSecondDirection" : true, "secondDirectionOppositeDirection" : true, "secondDirectionDepth" : 100 * mm});
        }
        {
            var Q0;
            {var subQ4=sQuery(id+"F10.wireOp",EDGE,"E18.top");Q0=makeQuery(id+"F10.imprint","IMPRINT",FACE,{"disambiguationData":[TD([[makeQuery(id+"F10.imprint","IMPRINT",EDGE,{"derivedFrom":subQ4}),-1.0]])]});}
            var sketch = newSketch(context, id + "F28", { "sketchPlane" : qUnion([Q0])});
            skLineSegment(sketch, "E42.bottom", {"start": v(3600, 1605) * mm, "end": v(3850, 1605) * mm});
            skLineSegment(sketch, "E42.top", {"start": v(3600, 1905) * mm, "end": v(3850, 1905) * mm});
            skLineSegment(sketch, "E42.left", {"start": v(3600, 1605) * mm, "end": v(3600, 1905) * mm});
            skLineSegment(sketch, "E42.right", {"start": v(3850, 1605) * mm, "end": v(3850, 1905) * mm});
            skSolve(sketch);
        }
        {
            var Q0;
            Q0=makeQuery(id+"F28.imprint","IMPRINT",FACE,{"disambiguationData":[TD([[makeQuery(id+"F28.imprint","IMPRINT",EDGE,{"derivedFrom":sQuery(id+"F28.wireOp",EDGE,"E42.bottom")}),1.0]])]});
            extrude(context, id + "F29", {"entities" : qUnion([Q0]), "operationType" : NewBodyOperationType.ADD, "depth" : 100 * mm, "offsetDistance" : 25 * mm});
        }
        {
            var Q0;
            Q0=makeQuery(id+"F29.opExtrude","CAP_FACE",FACE,{"disambiguationData":[OSD([sQuery(id+"F28.wireOp",EDGE,"E42.bottom"),sQuery(id+"F28.wireOp",EDGE,"E42.top"),sQuery(id+"F28.wireOp",EDGE,"E42.left"),sQuery(id+"F28.wireOp",EDGE,"E42.right")])],"isStart":false});
            var sketch = newSketch(context, id + "F30", { "sketchPlane" : qUnion([Q0])});
            skLineSegment(sketch, "E43.bottom", {"start": v(3660, 1765) * mm, "end": v(3630, 1765) * mm});
            skLineSegment(sketch, "E43.top", {"start": v(3660, 1785) * mm, "end": v(3630, 1785) * mm});
            skLineSegment(sketch, "E43.left", {"start": v(3660, 1765) * mm, "end": v(3660, 1785) * mm});
            skLineSegment(sketch, "E43.right", {"start": v(3630, 1765) * mm, "end": v(3630, 1785) * mm});
            skPoint(sketch, "E43.middle", {"position": v(3645, 1775) * mm});
            skLineSegment(sketch, "E44.0.1.0", {"start": v(3660, 1760) * mm, "end": v(3630, 1760) * mm});
            skPoint(sketch, "E44.0.1.1", {"position": v(3645, 1750) * mm});
            skLineSegment(sketch, "E44.0.1.2", {"start": v(3660, 1740) * mm, "end": v(3630, 1740) * mm});
            skLineSegment(sketch, "E44.0.1.3", {"start": v(3660, 1740) * mm, "end": v(3660, 1760) * mm});
            skLineSegment(sketch, "E44.0.1.4", {"start": v(3630, 1740) * mm, "end": v(3630, 1760) * mm});
            skLineSegment(sketch, "E44.0.2.0", {"start": v(3660, 1735) * mm, "end": v(3630, 1735) * mm});
            skPoint(sketch, "E44.0.2.1", {"position": v(3645, 1725) * mm});
            skLineSegment(sketch, "E44.0.2.2", {"start": v(3660, 1715) * mm, "end": v(3630, 1715) * mm});
            skLineSegment(sketch, "E44.0.2.3", {"start": v(3660, 1715) * mm, "end": v(3660, 1735) * mm});
            skLineSegment(sketch, "E44.0.2.4", {"start": v(3630, 1715) * mm, "end": v(3630, 1735) * mm});
            skLineSegment(sketch, "E44.0.3.0", {"start": v(3660, 1710) * mm, "end": v(3630, 1710) * mm});
            skPoint(sketch, "E44.0.3.1", {"position": v(3645, 1700) * mm});
            skLineSegment(sketch, "E44.0.3.2", {"start": v(3660, 1690) * mm, "end": v(3630, 1690) * mm});
            skLineSegment(sketch, "E44.0.3.3", {"start": v(3660, 1690) * mm, "end": v(3660, 1710) * mm});
            skLineSegment(sketch, "E44.0.3.4", {"start": v(3630, 1690) * mm, "end": v(3630, 1710) * mm});
            skLineSegment(sketch, "E44.0.4.0", {"start": v(3660, 1685) * mm, "end": v(3630, 1685) * mm});
            skPoint(sketch, "E44.0.4.1", {"position": v(3645, 1675) * mm});
            skLineSegment(sketch, "E44.0.4.2", {"start": v(3660, 1665) * mm, "end": v(3630, 1665) * mm});
            skLineSegment(sketch, "E44.0.4.3", {"start": v(3660, 1665) * mm, "end": v(3660, 1685) * mm});
            skLineSegment(sketch, "E44.0.4.4", {"start": v(3630, 1665) * mm, "end": v(3630, 1685) * mm});
            skLineSegment(sketch, "E44.1.0.0", {"start": v(3700, 1785) * mm, "end": v(3670, 1785) * mm});
            skPoint(sketch, "E44.1.0.1", {"position": v(3685, 1775) * mm});
            skLineSegment(sketch, "E44.1.0.2", {"start": v(3700, 1765) * mm, "end": v(3670, 1765) * mm});
            skLineSegment(sketch, "E44.1.0.3", {"start": v(3700, 1765) * mm, "end": v(3700, 1785) * mm});
            skLineSegment(sketch, "E44.1.0.4", {"start": v(3670, 1765) * mm, "end": v(3670, 1785) * mm});
            skLineSegment(sketch, "E44.1.1.0", {"start": v(3700, 1760) * mm, "end": v(3670, 1760) * mm});
            skPoint(sketch, "E44.1.1.1", {"position": v(3685, 1750) * mm});
            skLineSegment(sketch, "E44.1.1.2", {"start": v(3700, 1740) * mm, "end": v(3670, 1740) * mm});
            skLineSegment(sketch, "E44.1.1.3", {"start": v(3700, 1740) * mm, "end": v(3700, 1760) * mm});
            skLineSegment(sketch, "E44.1.1.4", {"start": v(3670, 1740) * mm, "end": v(3670, 1760) * mm});
            skLineSegment(sketch, "E44.1.2.0", {"start": v(3700, 1735) * mm, "end": v(3670, 1735) * mm});
            skPoint(sketch, "E44.1.2.1", {"position": v(3685, 1725) * mm});
            skLineSegment(sketch, "E44.1.2.2", {"start": v(3700, 1715) * mm, "end": v(3670, 1715) * mm});
            skLineSegment(sketch, "E44.1.2.3", {"start": v(3700, 1715) * mm, "end": v(3700, 1735) * mm});
            skLineSegment(sketch, "E44.1.2.4", {"start": v(3670, 1715) * mm, "end": v(3670, 1735) * mm});
            skLineSegment(sketch, "E44.1.3.0", {"start": v(3700, 1710) * mm, "end": v(3670, 1710) * mm});
            skPoint(sketch, "E44.1.3.1", {"position": v(3685, 1700) * mm});
            skLineSegment(sketch, "E44.1.3.2", {"start": v(3700, 1690) * mm, "end": v(3670, 1690) * mm});
            skLineSegment(sketch, "E44.1.3.3", {"start": v(3700, 1690) * mm, "end": v(3700, 1710) * mm});
            skLineSegment(sketch, "E44.1.3.4", {"start": v(3670, 1690) * mm, "end": v(3670, 1710) * mm});
            skLineSegment(sketch, "E44.1.4.0", {"start": v(3700, 1685) * mm, "end": v(3670, 1685) * mm});
            skPoint(sketch, "E44.1.4.1", {"position": v(3685, 1675) * mm});
            skLineSegment(sketch, "E44.1.4.2", {"start": v(3700, 1665) * mm, "end": v(3670, 1665) * mm});
            skLineSegment(sketch, "E44.1.4.3", {"start": v(3700, 1665) * mm, "end": v(3700, 1685) * mm});
            skLineSegment(sketch, "E44.1.4.4", {"start": v(3670, 1665) * mm, "end": v(3670, 1685) * mm});
            skLineSegment(sketch, "E44.2.0.0", {"start": v(3740, 1785) * mm, "end": v(3710, 1785) * mm});
            skPoint(sketch, "E44.2.0.1", {"position": v(3725, 1775) * mm});
            skLineSegment(sketch, "E44.2.0.2", {"start": v(3740, 1765) * mm, "end": v(3710, 1765) * mm});
            skLineSegment(sketch, "E44.2.0.3", {"start": v(3740, 1765) * mm, "end": v(3740, 1785) * mm});
            skLineSegment(sketch, "E44.2.0.4", {"start": v(3710, 1765) * mm, "end": v(3710, 1785) * mm});
            skLineSegment(sketch, "E44.2.1.0", {"start": v(3740, 1760) * mm, "end": v(3710, 1760) * mm});
            skPoint(sketch, "E44.2.1.1", {"position": v(3725, 1750) * mm});
            skLineSegment(sketch, "E44.2.1.2", {"start": v(3740, 1740) * mm, "end": v(3710, 1740) * mm});
            skLineSegment(sketch, "E44.2.1.3", {"start": v(3740, 1740) * mm, "end": v(3740, 1760) * mm});
            skLineSegment(sketch, "E44.2.1.4", {"start": v(3710, 1740) * mm, "end": v(3710, 1760) * mm});
            skLineSegment(sketch, "E44.2.2.0", {"start": v(3740, 1735) * mm, "end": v(3710, 1735) * mm});
            skPoint(sketch, "E44.2.2.1", {"position": v(3725, 1725) * mm});
            skLineSegment(sketch, "E44.2.2.2", {"start": v(3740, 1715) * mm, "end": v(3710, 1715) * mm});
            skLineSegment(sketch, "E44.2.2.3", {"start": v(3740, 1715) * mm, "end": v(3740, 1735) * mm});
            skLineSegment(sketch, "E44.2.2.4", {"start": v(3710, 1715) * mm, "end": v(3710, 1735) * mm});
            skLineSegment(sketch, "E44.2.3.0", {"start": v(3740, 1710) * mm, "end": v(3710, 1710) * mm});
            skPoint(sketch, "E44.2.3.1", {"position": v(3725, 1700) * mm});
            skLineSegment(sketch, "E44.2.3.2", {"start": v(3740, 1690) * mm, "end": v(3710, 1690) * mm});
            skLineSegment(sketch, "E44.2.3.3", {"start": v(3740, 1690) * mm, "end": v(3740, 1710) * mm});
            skLineSegment(sketch, "E44.2.3.4", {"start": v(3710, 1690) * mm, "end": v(3710, 1710) * mm});
            skLineSegment(sketch, "E44.2.4.0", {"start": v(3740, 1685) * mm, "end": v(3710, 1685) * mm});
            skPoint(sketch, "E44.2.4.1", {"position": v(3725, 1675) * mm});
            skLineSegment(sketch, "E44.2.4.2", {"start": v(3740, 1665) * mm, "end": v(3710, 1665) * mm});
            skLineSegment(sketch, "E44.2.4.3", {"start": v(3740, 1665) * mm, "end": v(3740, 1685) * mm});
            skLineSegment(sketch, "E44.2.4.4", {"start": v(3710, 1665) * mm, "end": v(3710, 1685) * mm});
            skLineSegment(sketch, "E44.3.0.0", {"start": v(3780, 1785) * mm, "end": v(3750, 1785) * mm});
            skPoint(sketch, "E44.3.0.1", {"position": v(3765, 1775) * mm});
            skLineSegment(sketch, "E44.3.0.2", {"start": v(3780, 1765) * mm, "end": v(3750, 1765) * mm});
            skLineSegment(sketch, "E44.3.0.3", {"start": v(3780, 1765) * mm, "end": v(3780, 1785) * mm});
            skLineSegment(sketch, "E44.3.0.4", {"start": v(3750, 1765) * mm, "end": v(3750, 1785) * mm});
            skLineSegment(sketch, "E44.3.1.0", {"start": v(3780, 1760) * mm, "end": v(3750, 1760) * mm});
            skPoint(sketch, "E44.3.1.1", {"position": v(3765, 1750) * mm});
            skLineSegment(sketch, "E44.3.1.2", {"start": v(3780, 1740) * mm, "end": v(3750, 1740) * mm});
            skLineSegment(sketch, "E44.3.1.3", {"start": v(3780, 1740) * mm, "end": v(3780, 1760) * mm});
            skLineSegment(sketch, "E44.3.1.4", {"start": v(3750, 1740) * mm, "end": v(3750, 1760) * mm});
            skLineSegment(sketch, "E44.3.2.0", {"start": v(3780, 1735) * mm, "end": v(3750, 1735) * mm});
            skPoint(sketch, "E44.3.2.1", {"position": v(3765, 1725) * mm});
            skLineSegment(sketch, "E44.3.2.2", {"start": v(3780, 1715) * mm, "end": v(3750, 1715) * mm});
            skLineSegment(sketch, "E44.3.2.3", {"start": v(3780, 1715) * mm, "end": v(3780, 1735) * mm});
            skLineSegment(sketch, "E44.3.2.4", {"start": v(3750, 1715) * mm, "end": v(3750, 1735) * mm});
            skLineSegment(sketch, "E44.3.3.0", {"start": v(3780, 1710) * mm, "end": v(3750, 1710) * mm});
            skPoint(sketch, "E44.3.3.1", {"position": v(3765, 1700) * mm});
            skLineSegment(sketch, "E44.3.3.2", {"start": v(3780, 1690) * mm, "end": v(3750, 1690) * mm});
            skLineSegment(sketch, "E44.3.3.3", {"start": v(3780, 1690) * mm, "end": v(3780, 1710) * mm});
            skLineSegment(sketch, "E44.3.3.4", {"start": v(3750, 1690) * mm, "end": v(3750, 1710) * mm});
            skLineSegment(sketch, "E44.3.4.0", {"start": v(3780, 1685) * mm, "end": v(3750, 1685) * mm});
            skPoint(sketch, "E44.3.4.1", {"position": v(3765, 1675) * mm});
            skLineSegment(sketch, "E44.3.4.2", {"start": v(3780, 1665) * mm, "end": v(3750, 1665) * mm});
            skLineSegment(sketch, "E44.3.4.3", {"start": v(3780, 1665) * mm, "end": v(3780, 1685) * mm});
            skLineSegment(sketch, "E44.3.4.4", {"start": v(3750, 1665) * mm, "end": v(3750, 1685) * mm});
            skLineSegment(sketch, "E44.4.0.0", {"start": v(3820, 1785) * mm, "end": v(3790, 1785) * mm});
            skPoint(sketch, "E44.4.0.1", {"position": v(3805, 1775) * mm});
            skLineSegment(sketch, "E44.4.0.2", {"start": v(3820, 1765) * mm, "end": v(3790, 1765) * mm});
            skLineSegment(sketch, "E44.4.0.3", {"start": v(3820, 1765) * mm, "end": v(3820, 1785) * mm});
            skLineSegment(sketch, "E44.4.0.4", {"start": v(3790, 1765) * mm, "end": v(3790, 1785) * mm});
            skLineSegment(sketch, "E44.4.1.0", {"start": v(3820, 1760) * mm, "end": v(3790, 1760) * mm});
            skPoint(sketch, "E44.4.1.1", {"position": v(3805, 1750) * mm});
            skLineSegment(sketch, "E44.4.1.2", {"start": v(3820, 1740) * mm, "end": v(3790, 1740) * mm});
            skLineSegment(sketch, "E44.4.1.3", {"start": v(3820, 1740) * mm, "end": v(3820, 1760) * mm});
            skLineSegment(sketch, "E44.4.1.4", {"start": v(3790, 1740) * mm, "end": v(3790, 1760) * mm});
            skLineSegment(sketch, "E44.4.2.0", {"start": v(3820, 1735) * mm, "end": v(3790, 1735) * mm});
            skPoint(sketch, "E44.4.2.1", {"position": v(3805, 1725) * mm});
            skLineSegment(sketch, "E44.4.2.2", {"start": v(3820, 1715) * mm, "end": v(3790, 1715) * mm});
            skLineSegment(sketch, "E44.4.2.3", {"start": v(3820, 1715) * mm, "end": v(3820, 1735) * mm});
            skLineSegment(sketch, "E44.4.2.4", {"start": v(3790, 1715) * mm, "end": v(3790, 1735) * mm});
            skLineSegment(sketch, "E44.4.3.0", {"start": v(3820, 1710) * mm, "end": v(3790, 1710) * mm});
            skPoint(sketch, "E44.4.3.1", {"position": v(3805, 1700) * mm});
            skLineSegment(sketch, "E44.4.3.2", {"start": v(3820, 1690) * mm, "end": v(3790, 1690) * mm});
            skLineSegment(sketch, "E44.4.3.3", {"start": v(3820, 1690) * mm, "end": v(3820, 1710) * mm});
            skLineSegment(sketch, "E44.4.3.4", {"start": v(3790, 1690) * mm, "end": v(3790, 1710) * mm});
            skLineSegment(sketch, "E44.4.4.0", {"start": v(3820, 1685) * mm, "end": v(3790, 1685) * mm});
            skPoint(sketch, "E44.4.4.1", {"position": v(3805, 1675) * mm});
            skLineSegment(sketch, "E44.4.4.2", {"start": v(3820, 1665) * mm, "end": v(3790, 1665) * mm});
            skLineSegment(sketch, "E44.4.4.3", {"start": v(3820, 1665) * mm, "end": v(3820, 1685) * mm});
            skLineSegment(sketch, "E44.4.4.4", {"start": v(3790, 1665) * mm, "end": v(3790, 1685) * mm});
            skLineSegment(sketch, "E44.direction1", {"start": v(3630, 1765) * mm, "end": v(3670, 1765) * mm, "construction": true});
            skLineSegment(sketch, "E44.direction2", {"start": v(3630, 1765) * mm, "end": v(3630, 1740) * mm, "construction": true});
            skSolve(sketch);
        }
        {
            var Q0;
            Q0 = qSketchRegion(id + "F30", true);
            extrude(context, id + "F31", {"entities" : qUnion([Q0]), "operationType" : NewBodyOperationType.ADD, "depth" : 10 * mm, "offsetDistance" : 25 * mm});
        }
        {
            var Q0;
            Q0=makeQuery(id+"F5.opExtrude","CAP_FACE",FACE,{"disambiguationData":[OSD([sQuery(id+"F4.wireOp",EDGE,"E13.bottom"),sQuery(id+"F4.wireOp",EDGE,"E13.top"),sQuery(id+"F4.wireOp",EDGE,"E13.left"),sQuery(id+"F4.wireOp",EDGE,"E13.right")])],"isStart":false});
            var sketch = newSketch(context, id + "F32", { "sketchPlane" : qUnion([Q0])});
            skLineSegment(sketch, "E45.bottom", {"start": v(3400, -700) * mm, "end": v(3600, -700) * mm});
            skLineSegment(sketch, "E45.top", {"start": v(3400, 700) * mm, "end": v(3600, 700) * mm});
            skLineSegment(sketch, "E45.left", {"start": v(3400, -700) * mm, "end": v(3400, 700) * mm});
            skLineSegment(sketch, "E45.right", {"start": v(3600, -700) * mm, "end": v(3600, 700) * mm});
            skPoint(sketch, "E45.middle", {"position": v(3500, 0) * mm});
            skPoint(sketch, "E46.1.0.0", {"position": v(1250, 0) * mm});
            skLineSegment(sketch, "E46.1.0.1", {"start": v(1150, -700) * mm, "end": v(1350, -700) * mm});
            skLineSegment(sketch, "E46.1.0.2", {"start": v(1350, -700) * mm, "end": v(1350, 700) * mm});
            skLineSegment(sketch, "E46.1.0.3", {"start": v(1150, 700) * mm, "end": v(1350, 700) * mm});
            skLineSegment(sketch, "E46.1.0.4", {"start": v(1150, -700) * mm, "end": v(1150, 700) * mm});
            skPoint(sketch, "E46.2.0.0", {"position": v(-1000, 0) * mm});
            skLineSegment(sketch, "E46.2.0.1", {"start": v(-1100, -700) * mm, "end": v(-900, -700) * mm});
            skLineSegment(sketch, "E46.2.0.2", {"start": v(-900, -700) * mm, "end": v(-900, 700) * mm});
            skLineSegment(sketch, "E46.2.0.3", {"start": v(-1100, 700) * mm, "end": v(-900, 700) * mm});
            skLineSegment(sketch, "E46.2.0.4", {"start": v(-1100, -700) * mm, "end": v(-1100, 700) * mm});
            skPoint(sketch, "E46.3.0.0", {"position": v(-3250, 0) * mm});
            skLineSegment(sketch, "E46.3.0.1", {"start": v(-3350, -700) * mm, "end": v(-3150, -700) * mm});
            skLineSegment(sketch, "E46.3.0.2", {"start": v(-3150, -700) * mm, "end": v(-3150, 700) * mm});
            skLineSegment(sketch, "E46.3.0.3", {"start": v(-3350, 700) * mm, "end": v(-3150, 700) * mm});
            skLineSegment(sketch, "E46.3.0.4", {"start": v(-3350, -700) * mm, "end": v(-3350, 700) * mm});
            skLineSegment(sketch, "E46.direction1", {"start": v(2400, -700) * mm, "end": v(150, -700) * mm, "construction": true});
            skSolve(sketch);
        }
        {
            var Q0;
            Q0 = qSketchRegion(id + "F32", true);
            extrude(context, id + "F33", {"entities" : qUnion([Q0]), "depth" : 80 * mm, "offsetDistance" : 25 * mm});
        }
    });
